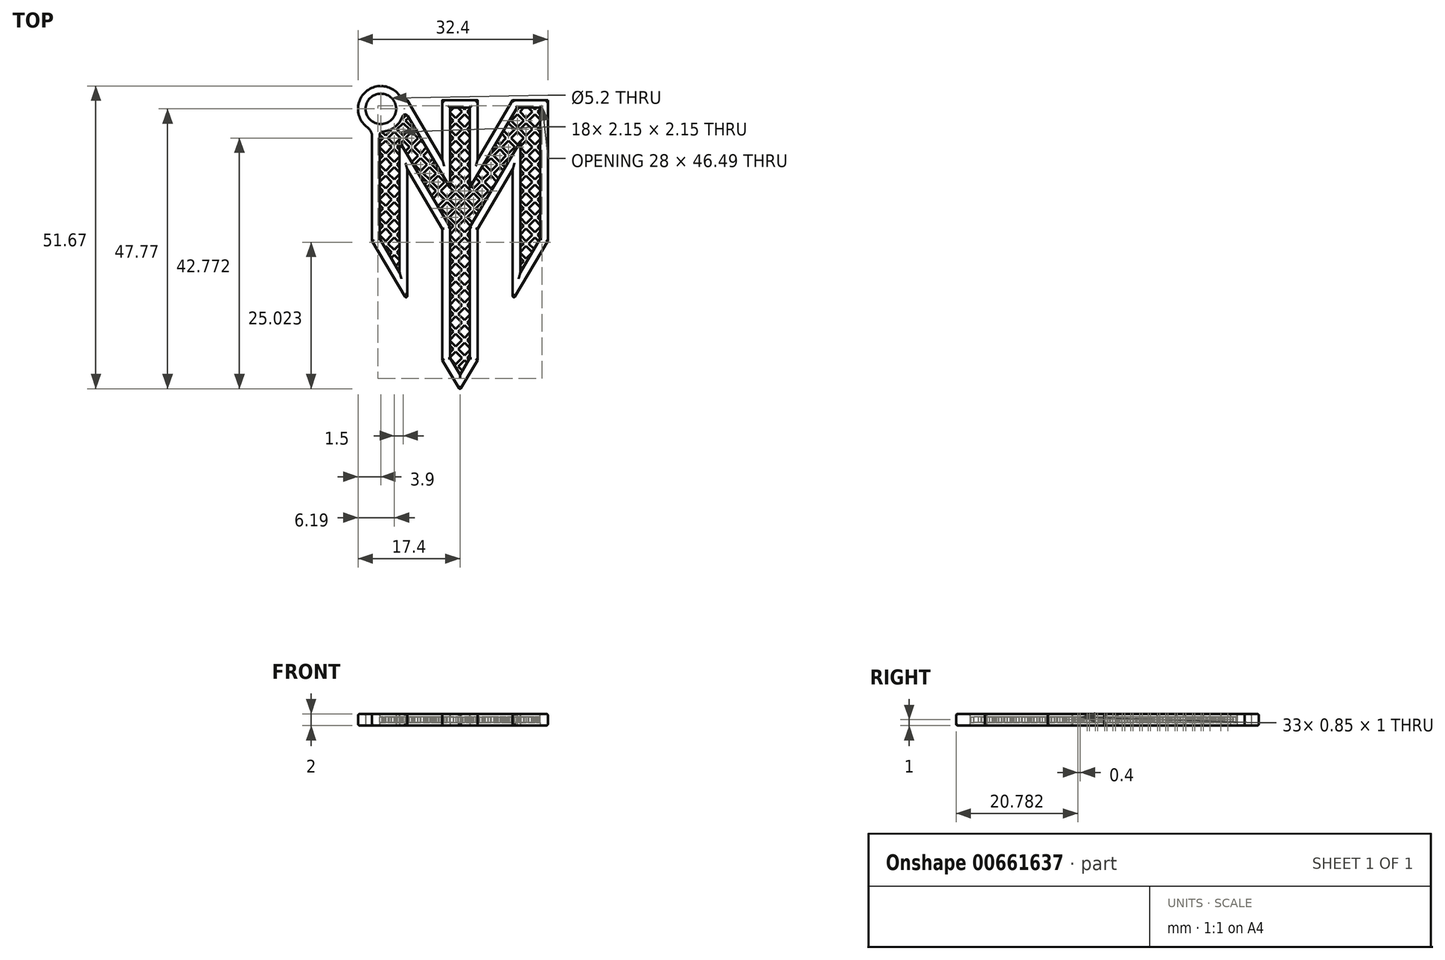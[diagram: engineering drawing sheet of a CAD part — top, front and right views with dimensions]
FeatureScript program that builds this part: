
annotation { "Feature Type Name" : "Feature", "Feature Type Description" : "" }
export const myFeature = defineFeature(function(context is Context, id is Id, definition is map)
    precondition{}
    {
        {
            var Q0;
            Q0=qCreatedBy(makeId("Top.planeOp"),FACE);
            var sketch = newSketch(context, id + "F0", { "sketchPlane" : qUnion([Q0])});
            skLineSegment(sketch, "E0", {"start": v(-3, 0) * mm, "end": v(3, 0) * mm});
            skLineSegment(sketch, "E1", {"start": v(-3, 0) * mm, "end": v(-3, -10.19) * mm});
            skLineSegment(sketch, "E2", {"start": v(-3, -10.19) * mm, "end": v(-9, 0) * mm});
            skLineSegment(sketch, "E3", {"start": v(-9, 0) * mm, "end": v(-15, 0) * mm});
            skLineSegment(sketch, "E4", {"start": v(3, 0) * mm, "end": v(3, -10.19) * mm});
            skLineSegment(sketch, "E5", {"start": v(3, -10.19) * mm, "end": v(9, 0) * mm});
            skLineSegment(sketch, "E6", {"start": v(9, 0) * mm, "end": v(15, 0) * mm});
            skLineSegment(sketch, "E7", {"start": v(0, 0) * mm, "end": v(0, -49.46) * mm, "construction": true});
            skLineSegment(sketch, "E8", {"start": v(-9, 0) * mm, "end": v(-3, 0) * mm, "construction": true});
            skLineSegment(sketch, "E9", {"start": v(3, 0) * mm, "end": v(9, 0) * mm, "construction": true});
            skLineSegment(sketch, "E10", {"start": v(-15, 0) * mm, "end": v(-15, -24) * mm});
            skLineSegment(sketch, "E11", {"start": v(-15, -24) * mm, "end": v(-9, -34.19) * mm});
            skLineSegment(sketch, "E12", {"start": v(-9, -34.19) * mm, "end": v(-9, -11.82) * mm});
            skLineSegment(sketch, "E13", {"start": v(-9, -11.82) * mm, "end": v(-3, -22) * mm});
            skLineSegment(sketch, "E14", {"start": v(-3.83, -8.78) * mm, "end": v(-9, -11.82) * mm, "construction": true});
            skLineSegment(sketch, "E15", {"start": v(15, 0) * mm, "end": v(15, -24) * mm});
            skLineSegment(sketch, "E16", {"start": v(15, -24) * mm, "end": v(9, -34.19) * mm});
            skLineSegment(sketch, "E17", {"start": v(9, -34.19) * mm, "end": v(9, -11.82) * mm});
            skLineSegment(sketch, "E18", {"start": v(9, -11.82) * mm, "end": v(3, -22) * mm});
            skLineSegment(sketch, "E19", {"start": v(-3, -22) * mm, "end": v(-3, -44.37) * mm});
            skLineSegment(sketch, "E20", {"start": v(-3, -44.37) * mm, "end": v(0, -49.46) * mm});
            skLineSegment(sketch, "E21", {"start": v(0, -49.46) * mm, "end": v(3, -44.37) * mm});
            skLineSegment(sketch, "E22", {"start": v(3, -44.37) * mm, "end": v(3, -22) * mm});
            skLineSegment(sketch, "E23", {"start": v(-9, -34.19) * mm, "end": v(-3, -44.37) * mm, "construction": true});
            skLineSegment(sketch, "E24", {"start": v(9, -34.19) * mm, "end": v(3, -44.37) * mm, "construction": true});
            skLineSegment(sketch, "E25", {"start": v(15, 0) * mm, "end": v(15, -6) * mm, "construction": true});
            skLineSegment(sketch, "E26", {"start": v(15, -6) * mm, "end": v(15, -12) * mm, "construction": true});
            skLineSegment(sketch, "E27", {"start": v(15, -12) * mm, "end": v(15, -18) * mm, "construction": true});
            skLineSegment(sketch, "E28", {"start": v(15, -18) * mm, "end": v(15, -24) * mm, "construction": true});
            skCircle(sketch, "E29", {"center": v(-13.5, -1.5) * mm, "radius": 2.6 * mm});
            skCircle(sketch, "E30", {"center": v(-13.5, -1.5) * mm, "radius": 3.9 * mm});
            skLineSegment(sketch, "E31", {"start": v(-13.5, 0) * mm, "end": v(-13.5, -1.5) * mm, "construction": true});
            skLineSegment(sketch, "E32", {"start": v(-15, -1.5) * mm, "end": v(-13.5, -1.5) * mm, "construction": true});
            skLineSegment(sketch, "E33.1", {"start": v(-1.7, -14.95) * mm, "end": v(-9.6, -1.54) * mm});
            skLineSegment(sketch, "E33.2", {"start": v(-1.7, -1.3) * mm, "end": v(-1.7, -14.95) * mm});
            skLineSegment(sketch, "E33.3", {"start": v(-1.7, -1.3) * mm, "end": v(1.7, -1.3) * mm});
            skLineSegment(sketch, "E33.4", {"start": v(1.7, -1.3) * mm, "end": v(1.7, -14.95) * mm});
            skLineSegment(sketch, "E33.5", {"start": v(-13.7, -5.4) * mm, "end": v(-13.7, -23.65) * mm});
            skLineSegment(sketch, "E33.6", {"start": v(1.7, -14.95) * mm, "end": v(9.74, -1.3) * mm});
            skLineSegment(sketch, "E33.7", {"start": v(9.74, -1.3) * mm, "end": v(13.7, -1.3) * mm});
            skLineSegment(sketch, "E33.8", {"start": v(13.7, -1.3) * mm, "end": v(13.7, -6) * mm});
            skLineSegment(sketch, "E33.9", {"start": v(13.7, -6) * mm, "end": v(13.7, -12) * mm});
            skLineSegment(sketch, "E33.10", {"start": v(13.7, -12) * mm, "end": v(13.7, -18) * mm});
            skLineSegment(sketch, "E33.11", {"start": v(13.7, -18) * mm, "end": v(13.7, -23.65) * mm});
            skLineSegment(sketch, "E33.12", {"start": v(-1.7, -21.65) * mm, "end": v(-1.7, -44.02) * mm});
            skLineSegment(sketch, "E33.13", {"start": v(-10.3, -7.05) * mm, "end": v(-1.7, -21.65) * mm});
            skLineSegment(sketch, "E33.14", {"start": v(-10.3, -29.42) * mm, "end": v(-10.3, -7.05) * mm});
            skLineSegment(sketch, "E33.15", {"start": v(-13.7, -23.65) * mm, "end": v(-10.3, -29.42) * mm});
            skLineSegment(sketch, "E33.16", {"start": v(-1.7, -44.02) * mm, "end": v(0, -46.9) * mm});
            skLineSegment(sketch, "E33.17", {"start": v(0, -46.9) * mm, "end": v(1.7, -44.02) * mm});
            skLineSegment(sketch, "E33.18", {"start": v(1.7, -44.02) * mm, "end": v(1.7, -21.65) * mm});
            skLineSegment(sketch, "E33.19", {"start": v(10.3, -7.05) * mm, "end": v(1.7, -21.65) * mm});
            skLineSegment(sketch, "E33.20", {"start": v(10.3, -29.42) * mm, "end": v(10.3, -7.05) * mm});
            skLineSegment(sketch, "E33.21", {"start": v(13.7, -23.65) * mm, "end": v(10.3, -29.42) * mm});
            skSolve(sketch);
        }
        {
            var Q0;
            Q0=makeQuery(id+"F0.imprint","IMPRINT",FACE,{"disambiguationData":[TD([[makeQuery(id+"F0.imprint","IMPRINT",EDGE,{"derivedFrom":sQuery(id+"F0.wireOp",EDGE,"E0")}),-1.0]])]});
            var Q1;
            {var subQ0=sQuery(id+"F0.wireOp",EDGE,"E30");var subQ2=sQuery(id+"F0.wireOp",EDGE,"E3");var subQ3=makeQuery(id+"F0.imprint","INTERSECT",VERTEX,{"derivedFrom":[subQ2,subQ0]});Q1=makeQuery(id+"F0.imprint","IMPRINT",FACE,{"disambiguationData":[TD([[makeQuery(id+"F0.imprint","IMPRINT",EDGE,{"disambiguationData":[TD([[subQ3,-1.0]])],"derivedFrom":subQ2}),1.0]])]});}
            var Q2;
            {var subQ0=sQuery(id+"F0.wireOp",EDGE,"E30");var subQ1=sQuery(id+"F0.wireOp",EDGE,"E3");var subQ2=makeQuery(id+"F0.imprint","INTERSECT",VERTEX,{"derivedFrom":[subQ1,subQ0]});Q2=makeQuery(id+"F0.imprint","IMPRINT",FACE,{"disambiguationData":[TD([[makeQuery(id+"F0.imprint","IMPRINT",EDGE,{"disambiguationData":[TD([[subQ2,-1.0]])],"derivedFrom":subQ1}),-1.0]])]});}
            extrude(context, id + "F1", {"entities" : qUnion([Q0, Q1, Q2]), "depth" : 2 * mm, "offsetDistance" : 25 * mm});
        }
        {
            var Q0;
            Q0=makeQuery(id+"F1.opExtrude","CAP_FACE",FACE,{"disambiguationData":[OSD([sQuery(id+"F0.wireOp",EDGE,"E0"),sQuery(id+"F0.wireOp",EDGE,"E1"),sQuery(id+"F0.wireOp",EDGE,"E2"),sQuery(id+"F0.wireOp",EDGE,"E3"),sQuery(id+"F0.wireOp",EDGE,"E4"),sQuery(id+"F0.wireOp",EDGE,"E5"),sQuery(id+"F0.wireOp",EDGE,"E6"),sQuery(id+"F0.wireOp",EDGE,"E10"),sQuery(id+"F0.wireOp",EDGE,"E11"),sQuery(id+"F0.wireOp",EDGE,"E12"),sQuery(id+"F0.wireOp",EDGE,"E13"),sQuery(id+"F0.wireOp",EDGE,"E15"),sQuery(id+"F0.wireOp",EDGE,"E16"),sQuery(id+"F0.wireOp",EDGE,"E17"),sQuery(id+"F0.wireOp",EDGE,"E18"),sQuery(id+"F0.wireOp",EDGE,"E19"),sQuery(id+"F0.wireOp",EDGE,"E20"),sQuery(id+"F0.wireOp",EDGE,"E21"),sQuery(id+"F0.wireOp",EDGE,"E22"),sQuery(id+"F0.wireOp",EDGE,"E29"),sQuery(id+"F0.wireOp",EDGE,"E30"),sQuery(id+"F0.wireOp",EDGE,"E33.0"),sQuery(id+"F0.wireOp",EDGE,"E33.1"),sQuery(id+"F0.wireOp",EDGE,"E33.2"),sQuery(id+"F0.wireOp",EDGE,"E33.3"),sQuery(id+"F0.wireOp",EDGE,"E33.4"),sQuery(id+"F0.wireOp",EDGE,"E33.5"),sQuery(id+"F0.wireOp",EDGE,"E33.6"),sQuery(id+"F0.wireOp",EDGE,"E33.7"),sQuery(id+"F0.wireOp",EDGE,"E33.8"),sQuery(id+"F0.wireOp",EDGE,"E33.9"),sQuery(id+"F0.wireOp",EDGE,"E33.10"),sQuery(id+"F0.wireOp",EDGE,"E33.11"),sQuery(id+"F0.wireOp",EDGE,"E33.12"),sQuery(id+"F0.wireOp",EDGE,"E33.13"),sQuery(id+"F0.wireOp",EDGE,"E33.14"),sQuery(id+"F0.wireOp",EDGE,"E33.15"),sQuery(id+"F0.wireOp",EDGE,"E33.16"),sQuery(id+"F0.wireOp",EDGE,"E33.17"),sQuery(id+"F0.wireOp",EDGE,"E33.18"),sQuery(id+"F0.wireOp",EDGE,"E33.19"),sQuery(id+"F0.wireOp",EDGE,"E33.20"),sQuery(id+"F0.wireOp",EDGE,"E33.21")])],"isStart":false});
            var sketch = newSketch(context, id + "F2", { "sketchPlane" : qUnion([Q0])});
            skArc(sketch, "E34.0.0", {"start": v(-9.9, 0) * mm, "mid": v(-16.26, 1.26) * mm, "end": v(-15, -5.1) * mm});
            skLineSegment(sketch, "E34.0.1", {"start": v(-15, -5.1) * mm, "end": v(-15, -24) * mm});
            skLineSegment(sketch, "E34.0.2", {"start": v(-15, -24) * mm, "end": v(-9, -34.19) * mm});
            skLineSegment(sketch, "E34.0.3", {"start": v(-9, -34.19) * mm, "end": v(-9, -11.82) * mm});
            skLineSegment(sketch, "E34.0.4", {"start": v(-9, -11.82) * mm, "end": v(-3, -22) * mm});
            skLineSegment(sketch, "E34.0.5", {"start": v(-3, -22) * mm, "end": v(-3, -44.37) * mm});
            skLineSegment(sketch, "E34.0.6", {"start": v(-3, -44.37) * mm, "end": v(0, -49.46) * mm});
            skLineSegment(sketch, "E34.0.7", {"start": v(0, -49.46) * mm, "end": v(3, -44.37) * mm});
            skLineSegment(sketch, "E34.0.8", {"start": v(3, -44.37) * mm, "end": v(3, -22) * mm});
            skLineSegment(sketch, "E34.0.9", {"start": v(3, -22) * mm, "end": v(9, -11.82) * mm});
            skLineSegment(sketch, "E34.0.10", {"start": v(9, -11.82) * mm, "end": v(9, -34.19) * mm});
            skLineSegment(sketch, "E34.0.11", {"start": v(9, -34.19) * mm, "end": v(15, -24) * mm});
            skLineSegment(sketch, "E34.0.12", {"start": v(15, -24) * mm, "end": v(15, 0) * mm});
            skLineSegment(sketch, "E34.0.13", {"start": v(15, 0) * mm, "end": v(9, 0) * mm});
            skLineSegment(sketch, "E34.0.14", {"start": v(9, 0) * mm, "end": v(3, -10.19) * mm});
            skLineSegment(sketch, "E34.0.15", {"start": v(3, -10.19) * mm, "end": v(3, 0) * mm});
            skLineSegment(sketch, "E34.0.16", {"start": v(3, 0) * mm, "end": v(-3, 0) * mm});
            skLineSegment(sketch, "E34.0.17", {"start": v(-3, 0) * mm, "end": v(-3, -10.19) * mm});
            skLineSegment(sketch, "E34.0.18", {"start": v(-3, -10.19) * mm, "end": v(-9, 0) * mm});
            skLineSegment(sketch, "E34.0.19", {"start": v(-9, 0) * mm, "end": v(-9.9, 0) * mm});
            skSolve(sketch);
        }
        {
            var Q0;
            Q0=makeQuery(id+"F1.opExtrude","SWEPT_EDGE",EDGE,{"disambiguationData":[OSD([sQuery(id+"F0.wireOp",EDGE,"E3"),sQuery(id+"F0.wireOp",EDGE,"E30")])]});
            var Q1;
            Q1=makeQuery(id+"F1.opExtrude","SWEPT_EDGE",EDGE,{"disambiguationData":[OSD([sQuery(id+"F0.wireOp",EDGE,"E10"),sQuery(id+"F0.wireOp",EDGE,"E30")])]});
            fillet(context, id + "F3", {"entities" : qUnion([Q0, Q1]), "radius" : 2 * mm, "tangentPropagation" : true, "defaultsChanged" : false, "vertexSettings" : [], "allowEdgeOverflow" : false});
        }
        {
            var Q0;
            Q0=makeQuery(id+"F1.opExtrude","SWEPT_EDGE",EDGE,{"disambiguationData":[OSD([sQuery(id+"F0.wireOp",EDGE,"E11"),sQuery(id+"F0.wireOp",EDGE,"E12")])]});
            var Q1;
            Q1=makeQuery(id+"F1.opExtrude","SWEPT_EDGE",EDGE,{"disambiguationData":[OSD([sQuery(id+"F0.wireOp",EDGE,"E16"),sQuery(id+"F0.wireOp",EDGE,"E17")])]});
            var Q2;
            Q2=makeQuery(id+"F1.opExtrude","SWEPT_EDGE",EDGE,{"disambiguationData":[OSD([sQuery(id+"F0.wireOp",EDGE,"E20"),sQuery(id+"F0.wireOp",EDGE,"E21")])]});
            fillet(context, id + "F4", {"entities" : qUnion([Q0, Q1, Q2]), "tangentPropagation" : true, "radius" : 0.2 * mm, "defaultsChanged" : false, "vertexSettings" : [], "allowEdgeOverflow" : false});
        }
        {
            var Q0;
            Q0=makeQuery(id+"F1.opExtrude","CAP_FACE",FACE,{"disambiguationData":[OSD([sQuery(id+"F0.wireOp",EDGE,"E0"),sQuery(id+"F0.wireOp",EDGE,"E1"),sQuery(id+"F0.wireOp",EDGE,"E2"),sQuery(id+"F0.wireOp",EDGE,"E3"),sQuery(id+"F0.wireOp",EDGE,"E4"),sQuery(id+"F0.wireOp",EDGE,"E5"),sQuery(id+"F0.wireOp",EDGE,"E6"),sQuery(id+"F0.wireOp",EDGE,"E10"),sQuery(id+"F0.wireOp",EDGE,"E11"),sQuery(id+"F0.wireOp",EDGE,"E12"),sQuery(id+"F0.wireOp",EDGE,"E13"),sQuery(id+"F0.wireOp",EDGE,"E15"),sQuery(id+"F0.wireOp",EDGE,"E16"),sQuery(id+"F0.wireOp",EDGE,"E17"),sQuery(id+"F0.wireOp",EDGE,"E18"),sQuery(id+"F0.wireOp",EDGE,"E19"),sQuery(id+"F0.wireOp",EDGE,"E20"),sQuery(id+"F0.wireOp",EDGE,"E21"),sQuery(id+"F0.wireOp",EDGE,"E22"),sQuery(id+"F0.wireOp",EDGE,"E29"),sQuery(id+"F0.wireOp",EDGE,"E30"),sQuery(id+"F0.wireOp",EDGE,"E33.0"),sQuery(id+"F0.wireOp",EDGE,"E33.1"),sQuery(id+"F0.wireOp",EDGE,"E33.2"),sQuery(id+"F0.wireOp",EDGE,"E33.3"),sQuery(id+"F0.wireOp",EDGE,"E33.4"),sQuery(id+"F0.wireOp",EDGE,"E33.5"),sQuery(id+"F0.wireOp",EDGE,"E33.6"),sQuery(id+"F0.wireOp",EDGE,"E33.7"),sQuery(id+"F0.wireOp",EDGE,"E33.8"),sQuery(id+"F0.wireOp",EDGE,"E33.9"),sQuery(id+"F0.wireOp",EDGE,"E33.10"),sQuery(id+"F0.wireOp",EDGE,"E33.11"),sQuery(id+"F0.wireOp",EDGE,"E33.12"),sQuery(id+"F0.wireOp",EDGE,"E33.13"),sQuery(id+"F0.wireOp",EDGE,"E33.14"),sQuery(id+"F0.wireOp",EDGE,"E33.15"),sQuery(id+"F0.wireOp",EDGE,"E33.16"),sQuery(id+"F0.wireOp",EDGE,"E33.17"),sQuery(id+"F0.wireOp",EDGE,"E33.18"),sQuery(id+"F0.wireOp",EDGE,"E33.19"),sQuery(id+"F0.wireOp",EDGE,"E33.20"),sQuery(id+"F0.wireOp",EDGE,"E33.21")])],"isStart":false});
            var sketch = newSketch(context, id + "F5", { "sketchPlane" : qUnion([Q0])});
            skLineSegment(sketch, "E35.0.0", {"start": v(-15, -24) * mm, "end": v(-9.37, -33.55) * mm});
            skArc(sketch, "E35.0.1", {"start": v(-9.37, -33.55) * mm, "mid": v(-9.15, -33.65) * mm, "end": v(-9, -33.45) * mm});
            skLineSegment(sketch, "E35.0.2", {"start": v(-9, -33.45) * mm, "end": v(-9, -11.82) * mm});
            skLineSegment(sketch, "E35.0.3", {"start": v(-9, -11.82) * mm, "end": v(-3, -22) * mm});
            skLineSegment(sketch, "E35.0.4", {"start": v(-3, -22) * mm, "end": v(-3, -44.37) * mm});
            skLineSegment(sketch, "E35.0.5", {"start": v(-3, -44.37) * mm, "end": v(-0.17, -49.17) * mm});
            skArc(sketch, "E35.0.6", {"start": v(-0.17, -49.17) * mm, "mid": v(0, -49.27) * mm, "end": v(0.17, -49.17) * mm});
            skLineSegment(sketch, "E35.0.7", {"start": v(0.17, -49.17) * mm, "end": v(3, -44.37) * mm});
            skLineSegment(sketch, "E35.0.8", {"start": v(3, -44.37) * mm, "end": v(3, -22) * mm});
            skLineSegment(sketch, "E35.0.9", {"start": v(3, -22) * mm, "end": v(9, -11.82) * mm});
            skLineSegment(sketch, "E35.0.10", {"start": v(9, -11.82) * mm, "end": v(9, -33.45) * mm});
            skArc(sketch, "E35.0.11", {"start": v(9, -33.45) * mm, "mid": v(9.15, -33.65) * mm, "end": v(9.37, -33.55) * mm});
            skLineSegment(sketch, "E35.0.12", {"start": v(9.37, -33.55) * mm, "end": v(15, -24) * mm});
            skLineSegment(sketch, "E35.0.13", {"start": v(15, -24) * mm, "end": v(15, 0) * mm});
            skLineSegment(sketch, "E35.0.14", {"start": v(15, 0) * mm, "end": v(9, 0) * mm});
            skLineSegment(sketch, "E35.0.15", {"start": v(9, 0) * mm, "end": v(3, -10.19) * mm});
            skLineSegment(sketch, "E35.0.16", {"start": v(3, -10.19) * mm, "end": v(3, 0) * mm});
            skLineSegment(sketch, "E35.0.17", {"start": v(3, 0) * mm, "end": v(-3, 0) * mm});
            skLineSegment(sketch, "E35.0.18", {"start": v(-3, 0) * mm, "end": v(-3, -10.19) * mm});
            skLineSegment(sketch, "E35.0.19", {"start": v(-3, -10.19) * mm, "end": v(-9, 0) * mm});
            skArc(sketch, "E35.0.20", {"start": v(-9, 0) * mm, "mid": v(-9.76, 0.26) * mm, "end": v(-10.35, 0.8) * mm});
            skArc(sketch, "E35.0.21", {"start": v(-10.35, 0.8) * mm, "mid": v(-16.25, 1.26) * mm, "end": v(-15.81, -4.64) * mm});
            skArc(sketch, "E35.0.22", {"start": v(-15.81, -4.64) * mm, "mid": v(-15.21, -5.35) * mm, "end": v(-15, -6.25) * mm});
            skLineSegment(sketch, "E35.0.23", {"start": v(-15, -6.25) * mm, "end": v(-15, -24) * mm});
            skLineSegment(sketch, "E36", {"start": v(1.83, -50.61) * mm, "end": v(-51.76, 2.97) * mm});
            skLineSegment(sketch, "E37", {"start": v(-52.83, 3.2) * mm, "end": v(1.75, -51.38) * mm});
            skLineSegment(sketch, "E38.1.0.0", {"start": v(-49.83, 3.2) * mm, "end": v(4.75, -51.38) * mm});
            skLineSegment(sketch, "E38.1.0.1", {"start": v(4.83, -50.61) * mm, "end": v(-48.76, 2.97) * mm});
            skLineSegment(sketch, "E38.2.0.0", {"start": v(-46.83, 3.2) * mm, "end": v(7.75, -51.38) * mm});
            skLineSegment(sketch, "E38.2.0.1", {"start": v(7.83, -50.61) * mm, "end": v(-45.76, 2.97) * mm});
            skLineSegment(sketch, "E38.3.0.0", {"start": v(-43.83, 3.2) * mm, "end": v(10.75, -51.38) * mm});
            skLineSegment(sketch, "E38.3.0.1", {"start": v(10.83, -50.61) * mm, "end": v(-42.76, 2.97) * mm});
            skLineSegment(sketch, "E38.4.0.0", {"start": v(-40.83, 3.2) * mm, "end": v(13.75, -51.38) * mm});
            skLineSegment(sketch, "E38.4.0.1", {"start": v(13.83, -50.61) * mm, "end": v(-39.76, 2.97) * mm});
            skLineSegment(sketch, "E38.5.0.0", {"start": v(-37.83, 3.2) * mm, "end": v(16.75, -51.38) * mm});
            skLineSegment(sketch, "E38.5.0.1", {"start": v(16.83, -50.61) * mm, "end": v(-36.76, 2.97) * mm});
            skLineSegment(sketch, "E38.6.0.0", {"start": v(-34.83, 3.2) * mm, "end": v(19.75, -51.38) * mm});
            skLineSegment(sketch, "E38.6.0.1", {"start": v(19.83, -50.61) * mm, "end": v(-33.76, 2.97) * mm});
            skLineSegment(sketch, "E38.7.0.0", {"start": v(-31.83, 3.2) * mm, "end": v(22.75, -51.38) * mm});
            skLineSegment(sketch, "E38.7.0.1", {"start": v(22.83, -50.61) * mm, "end": v(-30.76, 2.97) * mm});
            skLineSegment(sketch, "E38.8.0.0", {"start": v(-28.83, 3.2) * mm, "end": v(25.75, -51.38) * mm});
            skLineSegment(sketch, "E38.8.0.1", {"start": v(25.83, -50.61) * mm, "end": v(-27.76, 2.97) * mm});
            skLineSegment(sketch, "E38.9.0.0", {"start": v(-25.83, 3.2) * mm, "end": v(28.75, -51.38) * mm});
            skLineSegment(sketch, "E38.9.0.1", {"start": v(28.83, -50.61) * mm, "end": v(-24.76, 2.97) * mm});
            skLineSegment(sketch, "E38.10.0.0", {"start": v(-22.83, 3.2) * mm, "end": v(31.75, -51.38) * mm});
            skLineSegment(sketch, "E38.10.0.1", {"start": v(31.83, -50.61) * mm, "end": v(-21.76, 2.97) * mm});
            skLineSegment(sketch, "E38.11.0.0", {"start": v(-19.83, 3.2) * mm, "end": v(34.75, -51.38) * mm});
            skLineSegment(sketch, "E38.11.0.1", {"start": v(34.83, -50.61) * mm, "end": v(-18.76, 2.97) * mm});
            skLineSegment(sketch, "E38.12.0.0", {"start": v(-16.83, 3.2) * mm, "end": v(37.75, -51.38) * mm});
            skLineSegment(sketch, "E38.12.0.1", {"start": v(37.83, -50.61) * mm, "end": v(-15.76, 2.97) * mm});
            skLineSegment(sketch, "E38.13.0.0", {"start": v(-13.83, 3.2) * mm, "end": v(40.75, -51.38) * mm});
            skLineSegment(sketch, "E38.13.0.1", {"start": v(40.83, -50.61) * mm, "end": v(-12.76, 2.97) * mm});
            skLineSegment(sketch, "E38.14.0.0", {"start": v(-10.83, 3.2) * mm, "end": v(43.75, -51.38) * mm});
            skLineSegment(sketch, "E38.14.0.1", {"start": v(43.83, -50.61) * mm, "end": v(-9.76, 2.97) * mm});
            skLineSegment(sketch, "E38.15.0.0", {"start": v(-7.83, 3.2) * mm, "end": v(46.75, -51.38) * mm});
            skLineSegment(sketch, "E38.15.0.1", {"start": v(46.83, -50.61) * mm, "end": v(-6.76, 2.97) * mm});
            skLineSegment(sketch, "E38.16.0.0", {"start": v(-4.83, 3.2) * mm, "end": v(49.75, -51.38) * mm});
            skLineSegment(sketch, "E38.16.0.1", {"start": v(49.83, -50.61) * mm, "end": v(-3.76, 2.97) * mm});
            skLineSegment(sketch, "E38.17.0.0", {"start": v(-1.83, 3.2) * mm, "end": v(52.75, -51.38) * mm});
            skLineSegment(sketch, "E38.17.0.1", {"start": v(52.83, -50.61) * mm, "end": v(-0.76, 2.97) * mm});
            skLineSegment(sketch, "E38.18.0.0", {"start": v(1.17, 3.2) * mm, "end": v(55.75, -51.38) * mm});
            skLineSegment(sketch, "E38.18.0.1", {"start": v(55.83, -50.61) * mm, "end": v(2.24, 2.97) * mm});
            skLineSegment(sketch, "E38.19.0.0", {"start": v(4.17, 3.2) * mm, "end": v(58.75, -51.38) * mm});
            skLineSegment(sketch, "E38.19.0.1", {"start": v(58.83, -50.61) * mm, "end": v(5.24, 2.97) * mm});
            skLineSegment(sketch, "E38.direction1", {"start": v(1.75, -51.38) * mm, "end": v(4.75, -51.38) * mm, "construction": true});
            skLineSegment(sketch, "E39.0.20.0", {"start": v(7.17, 3.2) * mm, "end": v(61.75, -51.38) * mm});
            skLineSegment(sketch, "E39.3.20.0", {"start": v(61.83, -50.61) * mm, "end": v(8.24, 2.97) * mm});
            skLineSegment(sketch, "E40.0.21.0", {"start": v(10.17, 3.2) * mm, "end": v(64.75, -51.38) * mm});
            skLineSegment(sketch, "E40.3.21.0", {"start": v(64.83, -50.61) * mm, "end": v(11.24, 2.97) * mm});
            skSolve(sketch);
        }
        {
            var Q0;
            Q0=makeQuery(id+"F1.opExtrude","CAP_FACE",FACE,{"disambiguationData":[OSD([sQuery(id+"F0.wireOp",EDGE,"E0"),sQuery(id+"F0.wireOp",EDGE,"E1"),sQuery(id+"F0.wireOp",EDGE,"E2"),sQuery(id+"F0.wireOp",EDGE,"E3"),sQuery(id+"F0.wireOp",EDGE,"E4"),sQuery(id+"F0.wireOp",EDGE,"E5"),sQuery(id+"F0.wireOp",EDGE,"E6"),sQuery(id+"F0.wireOp",EDGE,"E10"),sQuery(id+"F0.wireOp",EDGE,"E11"),sQuery(id+"F0.wireOp",EDGE,"E12"),sQuery(id+"F0.wireOp",EDGE,"E13"),sQuery(id+"F0.wireOp",EDGE,"E15"),sQuery(id+"F0.wireOp",EDGE,"E16"),sQuery(id+"F0.wireOp",EDGE,"E17"),sQuery(id+"F0.wireOp",EDGE,"E18"),sQuery(id+"F0.wireOp",EDGE,"E19"),sQuery(id+"F0.wireOp",EDGE,"E20"),sQuery(id+"F0.wireOp",EDGE,"E21"),sQuery(id+"F0.wireOp",EDGE,"E22"),sQuery(id+"F0.wireOp",EDGE,"E29"),sQuery(id+"F0.wireOp",EDGE,"E30"),sQuery(id+"F0.wireOp",EDGE,"E33.0"),sQuery(id+"F0.wireOp",EDGE,"E33.1"),sQuery(id+"F0.wireOp",EDGE,"E33.2"),sQuery(id+"F0.wireOp",EDGE,"E33.3"),sQuery(id+"F0.wireOp",EDGE,"E33.4"),sQuery(id+"F0.wireOp",EDGE,"E33.5"),sQuery(id+"F0.wireOp",EDGE,"E33.6"),sQuery(id+"F0.wireOp",EDGE,"E33.7"),sQuery(id+"F0.wireOp",EDGE,"E33.8"),sQuery(id+"F0.wireOp",EDGE,"E33.9"),sQuery(id+"F0.wireOp",EDGE,"E33.10"),sQuery(id+"F0.wireOp",EDGE,"E33.11"),sQuery(id+"F0.wireOp",EDGE,"E33.12"),sQuery(id+"F0.wireOp",EDGE,"E33.13"),sQuery(id+"F0.wireOp",EDGE,"E33.14"),sQuery(id+"F0.wireOp",EDGE,"E33.15"),sQuery(id+"F0.wireOp",EDGE,"E33.16"),sQuery(id+"F0.wireOp",EDGE,"E33.17"),sQuery(id+"F0.wireOp",EDGE,"E33.18"),sQuery(id+"F0.wireOp",EDGE,"E33.19"),sQuery(id+"F0.wireOp",EDGE,"E33.20"),sQuery(id+"F0.wireOp",EDGE,"E33.21")])],"isStart":false});
            var sketch = newSketch(context, id + "F6", { "sketchPlane" : qUnion([Q0])});
            skLineSegment(sketch, "E41", {"start": v(0.42, -50.8) * mm, "end": v(54.44, 3.23) * mm});
            skLineSegment(sketch, "E42", {"start": v(-0.94, -51.3) * mm, "end": v(53.97, 3.6) * mm});
            skLineSegment(sketch, "E43.1.0.0", {"start": v(-3.94, -51.3) * mm, "end": v(50.97, 3.6) * mm});
            skLineSegment(sketch, "E43.1.0.1", {"start": v(-2.58, -50.8) * mm, "end": v(51.44, 3.23) * mm});
            skLineSegment(sketch, "E43.2.0.0", {"start": v(-6.94, -51.3) * mm, "end": v(47.97, 3.6) * mm});
            skLineSegment(sketch, "E43.2.0.1", {"start": v(-5.58, -50.8) * mm, "end": v(48.44, 3.23) * mm});
            skLineSegment(sketch, "E43.3.0.0", {"start": v(-9.94, -51.3) * mm, "end": v(44.97, 3.6) * mm});
            skLineSegment(sketch, "E43.3.0.1", {"start": v(-8.58, -50.8) * mm, "end": v(45.44, 3.23) * mm});
            skLineSegment(sketch, "E43.4.0.0", {"start": v(-12.94, -51.3) * mm, "end": v(41.97, 3.6) * mm});
            skLineSegment(sketch, "E43.4.0.1", {"start": v(-11.58, -50.8) * mm, "end": v(42.44, 3.23) * mm});
            skLineSegment(sketch, "E43.5.0.0", {"start": v(-15.94, -51.3) * mm, "end": v(38.97, 3.6) * mm});
            skLineSegment(sketch, "E43.5.0.1", {"start": v(-14.58, -50.8) * mm, "end": v(39.44, 3.23) * mm});
            skLineSegment(sketch, "E43.6.0.0", {"start": v(-18.94, -51.3) * mm, "end": v(35.97, 3.6) * mm});
            skLineSegment(sketch, "E43.6.0.1", {"start": v(-17.58, -50.8) * mm, "end": v(36.44, 3.23) * mm});
            skLineSegment(sketch, "E43.7.0.0", {"start": v(-21.94, -51.3) * mm, "end": v(32.97, 3.6) * mm});
            skLineSegment(sketch, "E43.7.0.1", {"start": v(-20.58, -50.8) * mm, "end": v(33.44, 3.23) * mm});
            skLineSegment(sketch, "E43.8.0.0", {"start": v(-24.94, -51.3) * mm, "end": v(29.97, 3.6) * mm});
            skLineSegment(sketch, "E43.8.0.1", {"start": v(-23.58, -50.8) * mm, "end": v(30.44, 3.23) * mm});
            skLineSegment(sketch, "E43.9.0.0", {"start": v(-27.94, -51.3) * mm, "end": v(26.97, 3.6) * mm});
            skLineSegment(sketch, "E43.9.0.1", {"start": v(-26.58, -50.8) * mm, "end": v(27.44, 3.23) * mm});
            skLineSegment(sketch, "E43.10.0.0", {"start": v(-30.94, -51.3) * mm, "end": v(23.97, 3.6) * mm});
            skLineSegment(sketch, "E43.10.0.1", {"start": v(-29.58, -50.8) * mm, "end": v(24.44, 3.23) * mm});
            skLineSegment(sketch, "E43.11.0.0", {"start": v(-33.94, -51.3) * mm, "end": v(20.97, 3.6) * mm});
            skLineSegment(sketch, "E43.11.0.1", {"start": v(-32.58, -50.8) * mm, "end": v(21.44, 3.23) * mm});
            skLineSegment(sketch, "E43.12.0.0", {"start": v(-36.94, -51.3) * mm, "end": v(17.97, 3.6) * mm});
            skLineSegment(sketch, "E43.12.0.1", {"start": v(-35.58, -50.8) * mm, "end": v(18.44, 3.23) * mm});
            skLineSegment(sketch, "E43.13.0.0", {"start": v(-39.94, -51.3) * mm, "end": v(14.97, 3.6) * mm});
            skLineSegment(sketch, "E43.13.0.1", {"start": v(-38.58, -50.8) * mm, "end": v(15.44, 3.23) * mm});
            skLineSegment(sketch, "E43.14.0.0", {"start": v(-42.94, -51.3) * mm, "end": v(11.97, 3.6) * mm});
            skLineSegment(sketch, "E43.14.0.1", {"start": v(-41.58, -50.8) * mm, "end": v(12.44, 3.23) * mm});
            skLineSegment(sketch, "E43.15.0.0", {"start": v(-45.94, -51.3) * mm, "end": v(8.97, 3.6) * mm});
            skLineSegment(sketch, "E43.15.0.1", {"start": v(-44.58, -50.8) * mm, "end": v(9.44, 3.23) * mm});
            skLineSegment(sketch, "E43.16.0.0", {"start": v(-48.94, -51.3) * mm, "end": v(5.97, 3.6) * mm});
            skLineSegment(sketch, "E43.16.0.1", {"start": v(-47.58, -50.8) * mm, "end": v(6.44, 3.23) * mm});
            skLineSegment(sketch, "E43.17.0.0", {"start": v(-51.94, -51.3) * mm, "end": v(2.97, 3.6) * mm});
            skLineSegment(sketch, "E43.17.0.1", {"start": v(-50.58, -50.8) * mm, "end": v(3.44, 3.23) * mm});
            skLineSegment(sketch, "E43.18.0.0", {"start": v(-54.94, -51.3) * mm, "end": v(-0.03, 3.6) * mm});
            skLineSegment(sketch, "E43.18.0.1", {"start": v(-53.58, -50.8) * mm, "end": v(0.44, 3.23) * mm});
            skLineSegment(sketch, "E43.19.0.0", {"start": v(-57.94, -51.3) * mm, "end": v(-3.03, 3.6) * mm});
            skLineSegment(sketch, "E43.19.0.1", {"start": v(-56.58, -50.8) * mm, "end": v(-2.56, 3.23) * mm});
            skLineSegment(sketch, "E43.direction1", {"start": v(-0.94, -51.3) * mm, "end": v(-3.94, -51.3) * mm, "construction": true});
            skLineSegment(sketch, "E44.0.20.0", {"start": v(-60.94, -51.3) * mm, "end": v(-6.03, 3.6) * mm});
            skLineSegment(sketch, "E44.3.20.0", {"start": v(-59.58, -50.8) * mm, "end": v(-5.56, 3.23) * mm});
            skLineSegment(sketch, "E44.0.21.0", {"start": v(-63.94, -51.3) * mm, "end": v(-9.03, 3.6) * mm});
            skLineSegment(sketch, "E44.3.21.0", {"start": v(-62.58, -50.8) * mm, "end": v(-8.56, 3.23) * mm});
            skSolve(sketch);
        }
        {
            var Q0;
            {var subQ0=sQuery(id+"F5.wireOp",EDGE,"E38.10.0.0");var subQ1=makeQuery(id+"F1.opExtrude","CAP_EDGE",EDGE,{"disambiguationData":[OSD([sQuery(id+"F0.wireOp",EDGE,"E33.5")])],"isStart":false});var subQ2=makeQuery(id+"F5.imprint","INTERSECT",VERTEX,{"derivedFrom":[subQ1,subQ0]});Q0=makeQuery(id+"F5.imprint","IMPRINT",FACE,{"disambiguationData":[TD([[makeQuery(id+"F5.imprint","IMPRINT",EDGE,{"disambiguationData":[TD([[subQ2,-1.0]])],"derivedFrom":subQ0}),1.0]])]});}
            var Q1;
            {var subQ0=sQuery(id+"F5.wireOp",EDGE,"E38.9.0.0");var subQ1=makeQuery(id+"F1.opExtrude","CAP_EDGE",EDGE,{"disambiguationData":[OSD([sQuery(id+"F0.wireOp",EDGE,"E33.5")])],"isStart":false});var subQ2=makeQuery(id+"F5.imprint","INTERSECT",VERTEX,{"derivedFrom":[subQ1,subQ0]});Q1=makeQuery(id+"F5.imprint","IMPRINT",FACE,{"disambiguationData":[TD([[makeQuery(id+"F5.imprint","IMPRINT",EDGE,{"disambiguationData":[TD([[subQ2,-1.0]])],"derivedFrom":subQ0}),1.0]])]});}
            var Q2;
            {var subQ0=sQuery(id+"F5.wireOp",EDGE,"E38.8.0.0");var subQ1=makeQuery(id+"F1.opExtrude","CAP_EDGE",EDGE,{"disambiguationData":[OSD([sQuery(id+"F0.wireOp",EDGE,"E33.5")])],"isStart":false});var subQ2=makeQuery(id+"F5.imprint","INTERSECT",VERTEX,{"derivedFrom":[subQ1,subQ0]});Q2=makeQuery(id+"F5.imprint","IMPRINT",FACE,{"disambiguationData":[TD([[makeQuery(id+"F5.imprint","IMPRINT",EDGE,{"disambiguationData":[TD([[subQ2,-1.0]])],"derivedFrom":subQ0}),1.0]])]});}
            var Q3;
            {var subQ0=sQuery(id+"F5.wireOp",EDGE,"E38.11.0.0");var subQ4=makeQuery(id+"F1.opExtrude","CAP_EDGE",EDGE,{"disambiguationData":[OSD([sQuery(id+"F0.wireOp",EDGE,"E33.19")])],"isStart":false});var subQ5=makeQuery(id+"F5.imprint","INTERSECT",VERTEX,{"derivedFrom":[subQ4,subQ0]});Q3=makeQuery(id+"F5.imprint","IMPRINT",FACE,{"disambiguationData":[TD([[makeQuery(id+"F5.imprint","IMPRINT",EDGE,{"disambiguationData":[TD([[subQ5,1.0]])],"derivedFrom":subQ4}),-1.0]])]});}
            var Q4;
            {var subQ0=sQuery(id+"F5.wireOp",EDGE,"E38.12.0.0");var subQ4=makeQuery(id+"F1.opExtrude","CAP_EDGE",EDGE,{"disambiguationData":[OSD([sQuery(id+"F0.wireOp",EDGE,"E33.1")])],"isStart":false});var subQ5=makeQuery(id+"F5.imprint","INTERSECT",VERTEX,{"derivedFrom":[subQ4,subQ0]});Q4=makeQuery(id+"F5.imprint","IMPRINT",FACE,{"disambiguationData":[TD([[makeQuery(id+"F5.imprint","IMPRINT",EDGE,{"disambiguationData":[TD([[subQ5,-1.0]])],"derivedFrom":subQ4}),1.0]])]});}
            var Q5;
            {var subQ5=makeQuery(id+"F1.opExtrude","CAP_EDGE",EDGE,{"disambiguationData":[OSD([sQuery(id+"F0.wireOp",EDGE,"E33.13")])],"isStart":false});var subQ7=sQuery(id+"F5.wireOp",EDGE,"E38.10.0.0");var subQ8=makeQuery(id+"F5.imprint","INTERSECT",VERTEX,{"derivedFrom":[subQ5,subQ7]});Q5=makeQuery(id+"F5.imprint","IMPRINT",FACE,{"disambiguationData":[TD([[makeQuery(id+"F5.imprint","IMPRINT",EDGE,{"disambiguationData":[TD([[subQ8,-1.0]])],"derivedFrom":subQ7}),1.0]])]});}
            var Q6;
            {var subQ0=sQuery(id+"F5.wireOp",EDGE,"E38.7.0.0");var subQ1=makeQuery(id+"F1.opExtrude","CAP_EDGE",EDGE,{"disambiguationData":[OSD([sQuery(id+"F0.wireOp",EDGE,"E33.5")])],"isStart":false});var subQ2=makeQuery(id+"F5.imprint","INTERSECT",VERTEX,{"derivedFrom":[subQ1,subQ0]});Q6=makeQuery(id+"F5.imprint","IMPRINT",FACE,{"disambiguationData":[TD([[makeQuery(id+"F5.imprint","IMPRINT",EDGE,{"disambiguationData":[TD([[subQ2,-1.0]])],"derivedFrom":subQ0}),1.0]])]});}
            var Q7;
            {var subQ0=sQuery(id+"F5.wireOp",EDGE,"E38.6.0.0");var subQ1=makeQuery(id+"F1.opExtrude","CAP_EDGE",EDGE,{"disambiguationData":[OSD([sQuery(id+"F0.wireOp",EDGE,"E33.5")])],"isStart":false});var subQ2=makeQuery(id+"F5.imprint","INTERSECT",VERTEX,{"derivedFrom":[subQ1,subQ0]});Q7=makeQuery(id+"F5.imprint","IMPRINT",FACE,{"disambiguationData":[TD([[makeQuery(id+"F5.imprint","IMPRINT",EDGE,{"disambiguationData":[TD([[subQ2,-1.0]])],"derivedFrom":subQ0}),1.0]])]});}
            var Q8;
            {var subQ0=sQuery(id+"F5.wireOp",EDGE,"E38.5.0.0");var subQ1=makeQuery(id+"F1.opExtrude","CAP_EDGE",EDGE,{"disambiguationData":[OSD([sQuery(id+"F0.wireOp",EDGE,"E33.5")])],"isStart":false});var subQ2=makeQuery(id+"F5.imprint","INTERSECT",VERTEX,{"derivedFrom":[subQ1,subQ0]});Q8=makeQuery(id+"F5.imprint","IMPRINT",FACE,{"disambiguationData":[TD([[makeQuery(id+"F5.imprint","IMPRINT",EDGE,{"disambiguationData":[TD([[subQ2,-1.0]])],"derivedFrom":subQ0}),1.0]])]});}
            var Q9;
            {var subQ0=sQuery(id+"F5.wireOp",EDGE,"E38.4.0.0");var subQ1=makeQuery(id+"F1.opExtrude","CAP_EDGE",EDGE,{"disambiguationData":[OSD([sQuery(id+"F0.wireOp",EDGE,"E33.15")])],"isStart":false});var subQ2=makeQuery(id+"F5.imprint","INTERSECT",VERTEX,{"derivedFrom":[subQ1,subQ0]});Q9=makeQuery(id+"F5.imprint","IMPRINT",FACE,{"disambiguationData":[TD([[makeQuery(id+"F5.imprint","IMPRINT",EDGE,{"disambiguationData":[TD([[subQ2,-1.0]])],"derivedFrom":subQ0}),1.0]])]});}
            var Q10;
            {var subQ0=sQuery(id+"F5.wireOp",EDGE,"E38.15.0.0");var subQ1=makeQuery(id+"F1.opExtrude","CAP_EDGE",EDGE,{"disambiguationData":[OSD([sQuery(id+"F0.wireOp",EDGE,"E33.2")])],"isStart":false});var subQ2=makeQuery(id+"F5.imprint","INTERSECT",VERTEX,{"derivedFrom":[subQ1,subQ0]});Q10=makeQuery(id+"F5.imprint","IMPRINT",FACE,{"disambiguationData":[TD([[makeQuery(id+"F5.imprint","IMPRINT",EDGE,{"disambiguationData":[TD([[subQ2,-1.0]])],"derivedFrom":subQ0}),1.0]])]});}
            var Q11;
            {var subQ0=sQuery(id+"F5.wireOp",EDGE,"E38.16.0.0");var subQ1=makeQuery(id+"F1.opExtrude","CAP_EDGE",EDGE,{"disambiguationData":[OSD([sQuery(id+"F0.wireOp",EDGE,"E33.3")])],"isStart":false});var subQ2=makeQuery(id+"F5.imprint","INTERSECT",VERTEX,{"derivedFrom":[subQ1,subQ0]});Q11=makeQuery(id+"F5.imprint","IMPRINT",FACE,{"disambiguationData":[TD([[makeQuery(id+"F5.imprint","IMPRINT",EDGE,{"disambiguationData":[TD([[subQ2,-1.0]])],"derivedFrom":subQ0}),1.0]])]});}
            var Q12;
            {var subQ0=sQuery(id+"F5.wireOp",EDGE,"E38.14.0.0");var subQ1=makeQuery(id+"F1.opExtrude","CAP_EDGE",EDGE,{"disambiguationData":[OSD([sQuery(id+"F0.wireOp",EDGE,"E33.2")])],"isStart":false});var subQ2=makeQuery(id+"F5.imprint","INTERSECT",VERTEX,{"derivedFrom":[subQ1,subQ0]});Q12=makeQuery(id+"F5.imprint","IMPRINT",FACE,{"disambiguationData":[TD([[makeQuery(id+"F5.imprint","IMPRINT",EDGE,{"disambiguationData":[TD([[subQ2,-1.0]])],"derivedFrom":subQ0}),1.0]])]});}
            var Q13;
            {var subQ0=sQuery(id+"F5.wireOp",EDGE,"E38.13.0.0");var subQ1=makeQuery(id+"F1.opExtrude","CAP_EDGE",EDGE,{"disambiguationData":[OSD([sQuery(id+"F0.wireOp",EDGE,"E33.2")])],"isStart":false});var subQ2=makeQuery(id+"F5.imprint","INTERSECT",VERTEX,{"derivedFrom":[subQ1,subQ0]});Q13=makeQuery(id+"F5.imprint","IMPRINT",FACE,{"disambiguationData":[TD([[makeQuery(id+"F5.imprint","IMPRINT",EDGE,{"disambiguationData":[TD([[subQ2,-1.0]])],"derivedFrom":subQ0}),1.0]])]});}
            var Q14;
            {var subQ0=sQuery(id+"F5.wireOp",EDGE,"E38.12.0.0");var subQ1=makeQuery(id+"F1.opExtrude","CAP_EDGE",EDGE,{"disambiguationData":[OSD([sQuery(id+"F0.wireOp",EDGE,"E33.2")])],"isStart":false});var subQ2=makeQuery(id+"F5.imprint","INTERSECT",VERTEX,{"derivedFrom":[subQ1,subQ0]});Q14=makeQuery(id+"F5.imprint","IMPRINT",FACE,{"disambiguationData":[TD([[makeQuery(id+"F5.imprint","IMPRINT",EDGE,{"disambiguationData":[TD([[subQ2,-1.0]])],"derivedFrom":subQ0}),1.0]])]});}
            var Q15;
            {var subQ0=sQuery(id+"F5.wireOp",EDGE,"E38.13.0.0");var subQ1=makeQuery(id+"F1.opExtrude","CAP_EDGE",EDGE,{"disambiguationData":[OSD([sQuery(id+"F0.wireOp",EDGE,"E33.6")])],"isStart":false});var subQ2=makeQuery(id+"F5.imprint","INTERSECT",VERTEX,{"derivedFrom":[subQ1,subQ0]});Q15=makeQuery(id+"F5.imprint","IMPRINT",FACE,{"disambiguationData":[TD([[makeQuery(id+"F5.imprint","IMPRINT",EDGE,{"disambiguationData":[TD([[subQ2,-1.0]])],"derivedFrom":subQ0}),1.0]])]});}
            var Q16;
            {var subQ0=sQuery(id+"F5.wireOp",EDGE,"E38.14.0.0");var subQ1=makeQuery(id+"F1.opExtrude","CAP_EDGE",EDGE,{"disambiguationData":[OSD([sQuery(id+"F0.wireOp",EDGE,"E33.6")])],"isStart":false});var subQ2=makeQuery(id+"F5.imprint","INTERSECT",VERTEX,{"derivedFrom":[subQ1,subQ0]});Q16=makeQuery(id+"F5.imprint","IMPRINT",FACE,{"disambiguationData":[TD([[makeQuery(id+"F5.imprint","IMPRINT",EDGE,{"disambiguationData":[TD([[subQ2,-1.0]])],"derivedFrom":subQ0}),1.0]])]});}
            var Q17;
            {var subQ0=sQuery(id+"F5.wireOp",EDGE,"E38.9.0.0");var subQ1=makeQuery(id+"F1.opExtrude","CAP_EDGE",EDGE,{"disambiguationData":[OSD([sQuery(id+"F0.wireOp",EDGE,"E33.13")])],"isStart":false});var subQ2=makeQuery(id+"F5.imprint","INTERSECT",VERTEX,{"derivedFrom":[subQ1,subQ0]});Q17=makeQuery(id+"F5.imprint","IMPRINT",FACE,{"disambiguationData":[TD([[makeQuery(id+"F5.imprint","IMPRINT",EDGE,{"disambiguationData":[TD([[subQ2,-1.0]])],"derivedFrom":subQ0}),1.0]])]});}
            var Q18;
            {var subQ0=sQuery(id+"F5.wireOp",EDGE,"E38.16.0.0");var subQ1=makeQuery(id+"F1.opExtrude","CAP_EDGE",EDGE,{"disambiguationData":[OSD([sQuery(id+"F0.wireOp",EDGE,"E33.6")])],"isStart":false});var subQ2=makeQuery(id+"F5.imprint","INTERSECT",VERTEX,{"derivedFrom":[subQ1,subQ0]});Q18=makeQuery(id+"F5.imprint","IMPRINT",FACE,{"disambiguationData":[TD([[makeQuery(id+"F5.imprint","IMPRINT",EDGE,{"disambiguationData":[TD([[subQ2,-1.0]])],"derivedFrom":subQ0}),1.0]])]});}
            var Q19;
            {var subQ0=sQuery(id+"F5.wireOp",EDGE,"E38.15.0.0");var subQ1=makeQuery(id+"F1.opExtrude","CAP_EDGE",EDGE,{"disambiguationData":[OSD([sQuery(id+"F0.wireOp",EDGE,"E33.6")])],"isStart":false});var subQ2=makeQuery(id+"F5.imprint","INTERSECT",VERTEX,{"derivedFrom":[subQ1,subQ0]});Q19=makeQuery(id+"F5.imprint","IMPRINT",FACE,{"disambiguationData":[TD([[makeQuery(id+"F5.imprint","IMPRINT",EDGE,{"disambiguationData":[TD([[subQ2,-1.0]])],"derivedFrom":subQ0}),1.0]])]});}
            var Q20;
            {var subQ0=sQuery(id+"F5.wireOp",EDGE,"E38.2.0.0");var subQ1=makeQuery(id+"F1.opExtrude","CAP_EDGE",EDGE,{"disambiguationData":[OSD([sQuery(id+"F0.wireOp",EDGE,"E33.12")])],"isStart":false});var subQ2=makeQuery(id+"F5.imprint","INTERSECT",VERTEX,{"derivedFrom":[subQ1,subQ0]});Q20=makeQuery(id+"F5.imprint","IMPRINT",FACE,{"disambiguationData":[TD([[makeQuery(id+"F5.imprint","IMPRINT",EDGE,{"disambiguationData":[TD([[subQ2,-1.0]])],"derivedFrom":subQ0}),1.0]])]});}
            var Q21;
            {var subQ0=sQuery(id+"F5.wireOp",EDGE,"E38.3.0.0");var subQ1=makeQuery(id+"F1.opExtrude","CAP_EDGE",EDGE,{"disambiguationData":[OSD([sQuery(id+"F0.wireOp",EDGE,"E33.12")])],"isStart":false});var subQ2=makeQuery(id+"F5.imprint","INTERSECT",VERTEX,{"derivedFrom":[subQ1,subQ0]});Q21=makeQuery(id+"F5.imprint","IMPRINT",FACE,{"disambiguationData":[TD([[makeQuery(id+"F5.imprint","IMPRINT",EDGE,{"disambiguationData":[TD([[subQ2,-1.0]])],"derivedFrom":subQ0}),1.0]])]});}
            var Q22;
            {var subQ0=sQuery(id+"F5.wireOp",EDGE,"E38.4.0.0");var subQ1=makeQuery(id+"F1.opExtrude","CAP_EDGE",EDGE,{"disambiguationData":[OSD([sQuery(id+"F0.wireOp",EDGE,"E33.12")])],"isStart":false});var subQ2=makeQuery(id+"F5.imprint","INTERSECT",VERTEX,{"derivedFrom":[subQ1,subQ0]});Q22=makeQuery(id+"F5.imprint","IMPRINT",FACE,{"disambiguationData":[TD([[makeQuery(id+"F5.imprint","IMPRINT",EDGE,{"disambiguationData":[TD([[subQ2,-1.0]])],"derivedFrom":subQ0}),1.0]])]});}
            var Q23;
            {var subQ0=sQuery(id+"F5.wireOp",EDGE,"E38.5.0.0");var subQ1=makeQuery(id+"F1.opExtrude","CAP_EDGE",EDGE,{"disambiguationData":[OSD([sQuery(id+"F0.wireOp",EDGE,"E33.12")])],"isStart":false});var subQ2=makeQuery(id+"F5.imprint","INTERSECT",VERTEX,{"derivedFrom":[subQ1,subQ0]});Q23=makeQuery(id+"F5.imprint","IMPRINT",FACE,{"disambiguationData":[TD([[makeQuery(id+"F5.imprint","IMPRINT",EDGE,{"disambiguationData":[TD([[subQ2,-1.0]])],"derivedFrom":subQ0}),1.0]])]});}
            var Q24;
            {var subQ0=sQuery(id+"F5.wireOp",EDGE,"E38.6.0.0");var subQ1=makeQuery(id+"F1.opExtrude","CAP_EDGE",EDGE,{"disambiguationData":[OSD([sQuery(id+"F0.wireOp",EDGE,"E33.12")])],"isStart":false});var subQ2=makeQuery(id+"F5.imprint","INTERSECT",VERTEX,{"derivedFrom":[subQ1,subQ0]});Q24=makeQuery(id+"F5.imprint","IMPRINT",FACE,{"disambiguationData":[TD([[makeQuery(id+"F5.imprint","IMPRINT",EDGE,{"disambiguationData":[TD([[subQ2,-1.0]])],"derivedFrom":subQ0}),1.0]])]});}
            var Q25;
            {var subQ0=sQuery(id+"F5.wireOp",EDGE,"E38.7.0.0");var subQ1=makeQuery(id+"F1.opExtrude","CAP_EDGE",EDGE,{"disambiguationData":[OSD([sQuery(id+"F0.wireOp",EDGE,"E33.12")])],"isStart":false});var subQ2=makeQuery(id+"F5.imprint","INTERSECT",VERTEX,{"derivedFrom":[subQ1,subQ0]});Q25=makeQuery(id+"F5.imprint","IMPRINT",FACE,{"disambiguationData":[TD([[makeQuery(id+"F5.imprint","IMPRINT",EDGE,{"disambiguationData":[TD([[subQ2,-1.0]])],"derivedFrom":subQ0}),1.0]])]});}
            var Q26;
            {var subQ0=sQuery(id+"F5.wireOp",EDGE,"E38.8.0.0");var subQ1=makeQuery(id+"F1.opExtrude","CAP_EDGE",EDGE,{"disambiguationData":[OSD([sQuery(id+"F0.wireOp",EDGE,"E33.12")])],"isStart":false});var subQ2=makeQuery(id+"F5.imprint","INTERSECT",VERTEX,{"derivedFrom":[subQ1,subQ0]});Q26=makeQuery(id+"F5.imprint","IMPRINT",FACE,{"disambiguationData":[TD([[makeQuery(id+"F5.imprint","IMPRINT",EDGE,{"disambiguationData":[TD([[subQ2,-1.0]])],"derivedFrom":subQ0}),1.0]])]});}
            var Q27;
            {var subQ0=sQuery(id+"F5.wireOp",EDGE,"E38.13.0.0");var subQ1=makeQuery(id+"F1.opExtrude","CAP_EDGE",EDGE,{"disambiguationData":[OSD([sQuery(id+"F0.wireOp",EDGE,"E33.20")])],"isStart":false});var subQ2=makeQuery(id+"F5.imprint","INTERSECT",VERTEX,{"derivedFrom":[subQ1,subQ0]});Q27=makeQuery(id+"F5.imprint","IMPRINT",FACE,{"disambiguationData":[TD([[makeQuery(id+"F5.imprint","IMPRINT",EDGE,{"disambiguationData":[TD([[subQ2,-1.0]])],"derivedFrom":subQ0}),1.0]])]});}
            var Q28;
            {var subQ0=sQuery(id+"F5.wireOp",EDGE,"E38.14.0.0");var subQ1=makeQuery(id+"F1.opExtrude","CAP_EDGE",EDGE,{"disambiguationData":[OSD([sQuery(id+"F0.wireOp",EDGE,"E33.20")])],"isStart":false});var subQ2=makeQuery(id+"F5.imprint","INTERSECT",VERTEX,{"derivedFrom":[subQ1,subQ0]});Q28=makeQuery(id+"F5.imprint","IMPRINT",FACE,{"disambiguationData":[TD([[makeQuery(id+"F5.imprint","IMPRINT",EDGE,{"disambiguationData":[TD([[subQ2,-1.0]])],"derivedFrom":subQ1}),-1.0]])]});}
            var Q29;
            {var subQ0=sQuery(id+"F5.wireOp",EDGE,"E38.15.0.0");var subQ1=makeQuery(id+"F1.opExtrude","CAP_EDGE",EDGE,{"disambiguationData":[OSD([sQuery(id+"F0.wireOp",EDGE,"E33.20")])],"isStart":false});var subQ2=makeQuery(id+"F5.imprint","INTERSECT",VERTEX,{"derivedFrom":[subQ1,subQ0]});Q29=makeQuery(id+"F5.imprint","IMPRINT",FACE,{"disambiguationData":[TD([[makeQuery(id+"F5.imprint","IMPRINT",EDGE,{"disambiguationData":[TD([[subQ2,-1.0]])],"derivedFrom":subQ1}),-1.0]])]});}
            var Q30;
            {var subQ0=sQuery(id+"F5.wireOp",EDGE,"E38.12.0.0");var subQ1=makeQuery(id+"F1.opExtrude","CAP_EDGE",EDGE,{"disambiguationData":[OSD([sQuery(id+"F0.wireOp",EDGE,"E33.20")])],"isStart":false});var subQ2=makeQuery(id+"F5.imprint","INTERSECT",VERTEX,{"derivedFrom":[subQ1,subQ0]});Q30=makeQuery(id+"F5.imprint","IMPRINT",FACE,{"disambiguationData":[TD([[makeQuery(id+"F5.imprint","IMPRINT",EDGE,{"disambiguationData":[TD([[subQ2,-1.0]])],"derivedFrom":subQ0}),1.0]])]});}
            var Q31;
            {var subQ0=sQuery(id+"F5.wireOp",EDGE,"E38.11.0.0");var subQ1=makeQuery(id+"F1.opExtrude","CAP_EDGE",EDGE,{"disambiguationData":[OSD([sQuery(id+"F0.wireOp",EDGE,"E33.20")])],"isStart":false});var subQ2=makeQuery(id+"F5.imprint","INTERSECT",VERTEX,{"derivedFrom":[subQ1,subQ0]});Q31=makeQuery(id+"F5.imprint","IMPRINT",FACE,{"disambiguationData":[TD([[makeQuery(id+"F5.imprint","IMPRINT",EDGE,{"disambiguationData":[TD([[subQ2,-1.0]])],"derivedFrom":subQ0}),1.0]])]});}
            var Q32;
            {var subQ0=sQuery(id+"F5.wireOp",EDGE,"E38.16.0.0");var subQ1=makeQuery(id+"F1.opExtrude","CAP_EDGE",EDGE,{"disambiguationData":[OSD([sQuery(id+"F0.wireOp",EDGE,"E33.20")])],"isStart":false});var subQ2=makeQuery(id+"F5.imprint","INTERSECT",VERTEX,{"derivedFrom":[subQ1,subQ0]});Q32=makeQuery(id+"F5.imprint","IMPRINT",FACE,{"disambiguationData":[TD([[makeQuery(id+"F5.imprint","IMPRINT",EDGE,{"disambiguationData":[TD([[subQ2,-1.0]])],"derivedFrom":subQ1}),-1.0]])]});}
            var Q33;
            {var subQ0=sQuery(id+"F5.wireOp",EDGE,"E38.17.0.0");var subQ1=makeQuery(id+"F1.opExtrude","CAP_EDGE",EDGE,{"disambiguationData":[OSD([sQuery(id+"F0.wireOp",EDGE,"E33.20")])],"isStart":false});var subQ2=makeQuery(id+"F5.imprint","INTERSECT",VERTEX,{"derivedFrom":[subQ1,subQ0]});Q33=makeQuery(id+"F5.imprint","IMPRINT",FACE,{"disambiguationData":[TD([[makeQuery(id+"F5.imprint","IMPRINT",EDGE,{"disambiguationData":[TD([[subQ2,-1.0]])],"derivedFrom":subQ1}),-1.0]])]});}
            var Q34;
            {var subQ0=sQuery(id+"F5.wireOp",EDGE,"E38.17.0.0");var subQ1=makeQuery(id+"F1.opExtrude","CAP_EDGE",EDGE,{"disambiguationData":[OSD([sQuery(id+"F0.wireOp",EDGE,"E33.6")])],"isStart":false});var subQ2=makeQuery(id+"F5.imprint","INTERSECT",VERTEX,{"derivedFrom":[subQ1,subQ0]});Q34=makeQuery(id+"F5.imprint","IMPRINT",FACE,{"disambiguationData":[TD([[makeQuery(id+"F5.imprint","IMPRINT",EDGE,{"disambiguationData":[TD([[subQ2,-1.0]])],"derivedFrom":subQ0}),1.0]])]});}
            var Q35;
            {var subQ0=sQuery(id+"F5.wireOp",EDGE,"E38.18.0.0");var subQ1=makeQuery(id+"F1.opExtrude","CAP_EDGE",EDGE,{"disambiguationData":[OSD([sQuery(id+"F0.wireOp",EDGE,"E33.6")])],"isStart":false});var subQ2=makeQuery(id+"F5.imprint","INTERSECT",VERTEX,{"derivedFrom":[subQ1,subQ0]});Q35=makeQuery(id+"F5.imprint","IMPRINT",FACE,{"disambiguationData":[TD([[makeQuery(id+"F5.imprint","IMPRINT",EDGE,{"disambiguationData":[TD([[subQ2,-1.0]])],"derivedFrom":subQ1}),-1.0]])]});}
            var Q36;
            {var subQ0=sQuery(id+"F5.wireOp",EDGE,"E38.19.0.0");var subQ1=makeQuery(id+"F1.opExtrude","CAP_EDGE",EDGE,{"disambiguationData":[OSD([sQuery(id+"F0.wireOp",EDGE,"E33.6")])],"isStart":false});var subQ2=makeQuery(id+"F5.imprint","INTERSECT",VERTEX,{"derivedFrom":[subQ1,subQ0]});Q36=makeQuery(id+"F5.imprint","IMPRINT",FACE,{"disambiguationData":[TD([[makeQuery(id+"F5.imprint","IMPRINT",EDGE,{"disambiguationData":[TD([[subQ2,-1.0]])],"derivedFrom":subQ1}),-1.0]])]});}
            var Q37;
            {var subQ0=sQuery(id+"F5.wireOp",EDGE,"E39.0.20.0");var subQ1=makeQuery(id+"F1.opExtrude","CAP_EDGE",EDGE,{"disambiguationData":[OSD([sQuery(id+"F0.wireOp",EDGE,"E33.7")])],"isStart":false});var subQ2=makeQuery(id+"F5.imprint","INTERSECT",VERTEX,{"derivedFrom":[subQ1,subQ0]});Q37=makeQuery(id+"F5.imprint","IMPRINT",FACE,{"disambiguationData":[TD([[makeQuery(id+"F5.imprint","IMPRINT",EDGE,{"disambiguationData":[TD([[subQ2,-1.0]])],"derivedFrom":subQ1}),-1.0]])]});}
            var Q38;
            {var subQ0=sQuery(id+"F5.wireOp",EDGE,"E38.1.0.1");var subQ1=makeQuery(id+"F1.opExtrude","CAP_EDGE",EDGE,{"disambiguationData":[OSD([sQuery(id+"F0.wireOp",EDGE,"E33.17")])],"isStart":false});var subQ2=makeQuery(id+"F5.imprint","INTERSECT",VERTEX,{"derivedFrom":[subQ1,subQ0]});Q38=makeQuery(id+"F5.imprint","IMPRINT",FACE,{"disambiguationData":[TD([[makeQuery(id+"F5.imprint","IMPRINT",EDGE,{"disambiguationData":[TD([[subQ2,-1.0]])],"derivedFrom":subQ0}),1.0]])]});}
            var Q39;
            {var subQ0=sQuery(id+"F5.wireOp",EDGE,"E38.10.0.1");var subQ1=makeQuery(id+"F1.opExtrude","CAP_EDGE",EDGE,{"disambiguationData":[OSD([sQuery(id+"F0.wireOp",EDGE,"E33.21")])],"isStart":false});var subQ2=makeQuery(id+"F5.imprint","INTERSECT",VERTEX,{"derivedFrom":[subQ1,subQ0]});Q39=makeQuery(id+"F5.imprint","IMPRINT",FACE,{"disambiguationData":[TD([[makeQuery(id+"F5.imprint","IMPRINT",EDGE,{"disambiguationData":[TD([[subQ2,-1.0]])],"derivedFrom":subQ0}),1.0]])]});}
            var Q40;
            {var subQ0=sQuery(id+"F5.wireOp",EDGE,"E38.3.0.0");var subQ1=makeQuery(id+"F1.opExtrude","CAP_EDGE",EDGE,{"disambiguationData":[OSD([sQuery(id+"F0.wireOp",EDGE,"E33.12")])],"isStart":false});var subQ2=makeQuery(id+"F5.imprint","INTERSECT",VERTEX,{"derivedFrom":[subQ1,subQ0]});Q40=makeQuery(id+"F5.imprint","IMPRINT",FACE,{"disambiguationData":[TD([[makeQuery(id+"F5.imprint","IMPRINT",EDGE,{"disambiguationData":[TD([[subQ2,-1.0]])],"derivedFrom":subQ0}),1.0]])]});}
            var Q41;
            {var subQ0=sQuery(id+"F5.wireOp",EDGE,"E38.11.0.0");var subQ1=sQuery(id+"F0.wireOp",EDGE,"E33.1");var subQ5=makeQuery(id+"F1.opExtrude","CAP_EDGE",EDGE,{"disambiguationData":[OSD([subQ1])],"isStart":false});var subQ6=makeQuery(id+"F5.imprint","INTERSECT",VERTEX,{"derivedFrom":[subQ5,subQ0]});Q41=makeQuery(id+"F5.imprint","IMPRINT",FACE,{"disambiguationData":[TD([[makeQuery(id+"F5.imprint","IMPRINT",EDGE,{"disambiguationData":[TD([[subQ6,-1.0]])],"derivedFrom":subQ5}),1.0]])]});}
            extrude(context, id + "F7", {"entities" : qUnion([Q0, Q1, Q2, Q3, Q4, Q5, Q6, Q7, Q8, Q9, Q10, Q11, Q12, Q13, Q14, Q15, Q16, Q17, Q18, Q19, Q20, Q21, Q22, Q23, Q24, Q25, Q26, Q27, Q28, Q29, Q30, Q31, Q32, Q33, Q34, Q35, Q36, Q37, Q38, Q39, Q40, Q41]), "operationType" : NewBodyOperationType.ADD, "oppositeDirection" : true, "depth" : 2 * mm, "offsetDistance" : 25 * mm});
        }
        {
            var Q0;
            {var subQ0=sQuery(id+"F6.wireOp",EDGE,"E43.18.0.0");var subQ1=makeQuery(id+"F1.opExtrude","CAP_EDGE",EDGE,{"disambiguationData":[OSD([sQuery(id+"F0.wireOp",EDGE,"E33.5")])],"isStart":false});var subQ2=makeQuery(id+"F6.imprint","INTERSECT",VERTEX,{"derivedFrom":[subQ1,subQ0]});Q0=makeQuery(id+"F6.imprint","IMPRINT",FACE,{"disambiguationData":[TD([[makeQuery(id+"F6.imprint","IMPRINT",EDGE,{"disambiguationData":[TD([[subQ2,-1.0]])],"derivedFrom":subQ0}),-1.0]])]});}
            var Q1;
            {var subQ2=sQuery(id+"F0.wireOp",EDGE,"E33.5");var subQ8=sQuery(id+"F6.wireOp",EDGE,"E43.19.0.1");var subQ10=makeQuery(id+"F1.opExtrude","CAP_EDGE",EDGE,{"disambiguationData":[OSD([subQ2])],"isStart":false});var subQ11=makeQuery(id+"F6.imprint","INTERSECT",VERTEX,{"derivedFrom":[subQ10,subQ8]});Q1=makeQuery(id+"F6.imprint","IMPRINT",FACE,{"disambiguationData":[TD([[makeQuery(id+"F6.imprint","IMPRINT",EDGE,{"disambiguationData":[TD([[subQ11,-1.0]])],"derivedFrom":subQ8}),1.0]])]});}
            var Q2;
            {var subQ0=sQuery(id+"F6.wireOp",EDGE,"E43.17.0.0");var subQ1=makeQuery(id+"F1.opExtrude","CAP_EDGE",EDGE,{"disambiguationData":[OSD([sQuery(id+"F0.wireOp",EDGE,"E33.13")])],"isStart":false});var subQ2=makeQuery(id+"F6.imprint","INTERSECT",VERTEX,{"derivedFrom":[subQ1,subQ0]});Q2=makeQuery(id+"F6.imprint","IMPRINT",FACE,{"disambiguationData":[TD([[makeQuery(id+"F6.imprint","IMPRINT",EDGE,{"disambiguationData":[TD([[subQ2,-1.0]])],"derivedFrom":subQ0}),-1.0]])]});}
            var Q3;
            {var subQ0=sQuery(id+"F6.wireOp",EDGE,"E43.17.0.0");var subQ1=makeQuery(id+"F1.opExtrude","CAP_EDGE",EDGE,{"disambiguationData":[OSD([sQuery(id+"F0.wireOp",EDGE,"E33.5")])],"isStart":false});var subQ2=makeQuery(id+"F6.imprint","INTERSECT",VERTEX,{"derivedFrom":[subQ1,subQ0]});Q3=makeQuery(id+"F6.imprint","IMPRINT",FACE,{"disambiguationData":[TD([[makeQuery(id+"F6.imprint","IMPRINT",EDGE,{"disambiguationData":[TD([[subQ2,-1.0]])],"derivedFrom":subQ0}),-1.0]])]});}
            var Q4;
            {var subQ0=sQuery(id+"F6.wireOp",EDGE,"E43.16.0.0");var subQ1=makeQuery(id+"F1.opExtrude","CAP_EDGE",EDGE,{"disambiguationData":[OSD([sQuery(id+"F0.wireOp",EDGE,"E33.5")])],"isStart":false});var subQ2=makeQuery(id+"F6.imprint","INTERSECT",VERTEX,{"derivedFrom":[subQ1,subQ0]});Q4=makeQuery(id+"F6.imprint","IMPRINT",FACE,{"disambiguationData":[TD([[makeQuery(id+"F6.imprint","IMPRINT",EDGE,{"disambiguationData":[TD([[subQ2,-1.0]])],"derivedFrom":subQ0}),-1.0]])]});}
            var Q5;
            {var subQ0=sQuery(id+"F6.wireOp",EDGE,"E43.15.0.0");var subQ1=makeQuery(id+"F1.opExtrude","CAP_EDGE",EDGE,{"disambiguationData":[OSD([sQuery(id+"F0.wireOp",EDGE,"E33.5")])],"isStart":false});var subQ2=makeQuery(id+"F6.imprint","INTERSECT",VERTEX,{"derivedFrom":[subQ1,subQ0]});Q5=makeQuery(id+"F6.imprint","IMPRINT",FACE,{"disambiguationData":[TD([[makeQuery(id+"F6.imprint","IMPRINT",EDGE,{"disambiguationData":[TD([[subQ2,-1.0]])],"derivedFrom":subQ0}),-1.0]])]});}
            var Q6;
            {var subQ0=sQuery(id+"F6.wireOp",EDGE,"E43.14.0.0");var subQ1=makeQuery(id+"F1.opExtrude","CAP_EDGE",EDGE,{"disambiguationData":[OSD([sQuery(id+"F0.wireOp",EDGE,"E33.5")])],"isStart":false});var subQ2=makeQuery(id+"F6.imprint","INTERSECT",VERTEX,{"derivedFrom":[subQ1,subQ0]});Q6=makeQuery(id+"F6.imprint","IMPRINT",FACE,{"disambiguationData":[TD([[makeQuery(id+"F6.imprint","IMPRINT",EDGE,{"disambiguationData":[TD([[subQ2,-1.0]])],"derivedFrom":subQ0}),-1.0]])]});}
            var Q7;
            {var subQ0=sQuery(id+"F6.wireOp",EDGE,"E43.13.0.0");var subQ1=makeQuery(id+"F1.opExtrude","CAP_EDGE",EDGE,{"disambiguationData":[OSD([sQuery(id+"F0.wireOp",EDGE,"E33.15")])],"isStart":false});var subQ2=makeQuery(id+"F6.imprint","INTERSECT",VERTEX,{"derivedFrom":[subQ1,subQ0]});Q7=makeQuery(id+"F6.imprint","IMPRINT",FACE,{"disambiguationData":[TD([[makeQuery(id+"F6.imprint","IMPRINT",EDGE,{"disambiguationData":[TD([[subQ2,-1.0]])],"derivedFrom":subQ0}),-1.0]])]});}
            var Q8;
            {var subQ0=sQuery(id+"F6.wireOp",EDGE,"E43.12.0.0");var subQ1=makeQuery(id+"F1.opExtrude","CAP_EDGE",EDGE,{"disambiguationData":[OSD([sQuery(id+"F0.wireOp",EDGE,"E33.15")])],"isStart":false});var subQ2=makeQuery(id+"F6.imprint","INTERSECT",VERTEX,{"derivedFrom":[subQ1,subQ0]});Q8=makeQuery(id+"F6.imprint","IMPRINT",FACE,{"disambiguationData":[TD([[makeQuery(id+"F6.imprint","IMPRINT",EDGE,{"disambiguationData":[TD([[subQ2,-1.0]])],"derivedFrom":subQ0}),-1.0]])]});}
            var Q9;
            {var subQ0=sQuery(id+"F6.wireOp",EDGE,"E43.16.0.0");var subQ1=makeQuery(id+"F1.opExtrude","CAP_EDGE",EDGE,{"disambiguationData":[OSD([sQuery(id+"F0.wireOp",EDGE,"E33.13")])],"isStart":false});var subQ2=makeQuery(id+"F6.imprint","INTERSECT",VERTEX,{"derivedFrom":[subQ1,subQ0]});Q9=makeQuery(id+"F6.imprint","IMPRINT",FACE,{"disambiguationData":[TD([[makeQuery(id+"F6.imprint","IMPRINT",EDGE,{"disambiguationData":[TD([[subQ2,-1.0]])],"derivedFrom":subQ0}),-1.0]])]});}
            var Q10;
            {var subQ0=sQuery(id+"F6.wireOp",EDGE,"E43.15.0.0");var subQ1=makeQuery(id+"F1.opExtrude","CAP_EDGE",EDGE,{"disambiguationData":[OSD([sQuery(id+"F0.wireOp",EDGE,"E33.13")])],"isStart":false});var subQ2=makeQuery(id+"F6.imprint","INTERSECT",VERTEX,{"derivedFrom":[subQ1,subQ0]});Q10=makeQuery(id+"F6.imprint","IMPRINT",FACE,{"disambiguationData":[TD([[makeQuery(id+"F6.imprint","IMPRINT",EDGE,{"disambiguationData":[TD([[subQ2,-1.0]])],"derivedFrom":subQ0}),-1.0]])]});}
            var Q11;
            {var subQ0=sQuery(id+"F6.wireOp",EDGE,"E43.14.0.0");var subQ1=makeQuery(id+"F1.opExtrude","CAP_EDGE",EDGE,{"disambiguationData":[OSD([sQuery(id+"F0.wireOp",EDGE,"E33.13")])],"isStart":false});var subQ2=makeQuery(id+"F6.imprint","INTERSECT",VERTEX,{"derivedFrom":[subQ1,subQ0]});Q11=makeQuery(id+"F6.imprint","IMPRINT",FACE,{"disambiguationData":[TD([[makeQuery(id+"F6.imprint","IMPRINT",EDGE,{"disambiguationData":[TD([[subQ2,-1.0]])],"derivedFrom":subQ0}),-1.0]])]});}
            var Q12;
            {var subQ0=sQuery(id+"F6.wireOp",EDGE,"E43.13.0.0");var subQ1=makeQuery(id+"F1.opExtrude","CAP_EDGE",EDGE,{"disambiguationData":[OSD([sQuery(id+"F0.wireOp",EDGE,"E33.13")])],"isStart":false});var subQ2=makeQuery(id+"F6.imprint","INTERSECT",VERTEX,{"derivedFrom":[subQ1,subQ0]});Q12=makeQuery(id+"F6.imprint","IMPRINT",FACE,{"disambiguationData":[TD([[makeQuery(id+"F6.imprint","IMPRINT",EDGE,{"disambiguationData":[TD([[subQ2,-1.0]])],"derivedFrom":subQ0}),-1.0]])]});}
            var Q13;
            {var subQ0=sQuery(id+"F6.wireOp",EDGE,"E43.12.0.0");var subQ1=makeQuery(id+"F1.opExtrude","CAP_EDGE",EDGE,{"disambiguationData":[OSD([sQuery(id+"F0.wireOp",EDGE,"E33.13")])],"isStart":false});var subQ2=makeQuery(id+"F6.imprint","INTERSECT",VERTEX,{"derivedFrom":[subQ1,subQ0]});Q13=makeQuery(id+"F6.imprint","IMPRINT",FACE,{"disambiguationData":[TD([[makeQuery(id+"F6.imprint","IMPRINT",EDGE,{"disambiguationData":[TD([[subQ2,-1.0]])],"derivedFrom":subQ0}),-1.0]])]});}
            var Q14;
            {var subQ0=sQuery(id+"F6.wireOp",EDGE,"E43.13.0.0");var subQ1=makeQuery(id+"F1.opExtrude","CAP_EDGE",EDGE,{"disambiguationData":[OSD([sQuery(id+"F0.wireOp",EDGE,"E33.2")])],"isStart":false});var subQ2=makeQuery(id+"F6.imprint","INTERSECT",VERTEX,{"derivedFrom":[subQ1,subQ0]});Q14=makeQuery(id+"F6.imprint","IMPRINT",FACE,{"disambiguationData":[TD([[makeQuery(id+"F6.imprint","IMPRINT",EDGE,{"disambiguationData":[TD([[subQ2,-1.0]])],"derivedFrom":subQ0}),-1.0]])]});}
            var Q15;
            {var subQ0=sQuery(id+"F6.wireOp",EDGE,"E43.14.0.0");var subQ1=makeQuery(id+"F1.opExtrude","CAP_EDGE",EDGE,{"disambiguationData":[OSD([sQuery(id+"F0.wireOp",EDGE,"E33.2")])],"isStart":false});var subQ2=makeQuery(id+"F6.imprint","INTERSECT",VERTEX,{"derivedFrom":[subQ1,subQ0]});Q15=makeQuery(id+"F6.imprint","IMPRINT",FACE,{"disambiguationData":[TD([[makeQuery(id+"F6.imprint","IMPRINT",EDGE,{"disambiguationData":[TD([[subQ2,-1.0]])],"derivedFrom":subQ0}),-1.0]])]});}
            var Q16;
            {var subQ0=sQuery(id+"F6.wireOp",EDGE,"E43.15.0.0");var subQ1=makeQuery(id+"F1.opExtrude","CAP_EDGE",EDGE,{"disambiguationData":[OSD([sQuery(id+"F0.wireOp",EDGE,"E33.2")])],"isStart":false});var subQ2=makeQuery(id+"F6.imprint","INTERSECT",VERTEX,{"derivedFrom":[subQ1,subQ0]});Q16=makeQuery(id+"F6.imprint","IMPRINT",FACE,{"disambiguationData":[TD([[makeQuery(id+"F6.imprint","IMPRINT",EDGE,{"disambiguationData":[TD([[subQ2,-1.0]])],"derivedFrom":subQ0}),-1.0]])]});}
            var Q17;
            {var subQ5=sQuery(id+"F6.wireOp",EDGE,"E43.16.0.0");var subQ7=makeQuery(id+"F1.opExtrude","CAP_EDGE",EDGE,{"disambiguationData":[OSD([sQuery(id+"F0.wireOp",EDGE,"E33.2")])],"isStart":false});var subQ9=makeQuery(id+"F6.imprint","INTERSECT",VERTEX,{"derivedFrom":[subQ7,subQ5]});Q17=makeQuery(id+"F6.imprint","IMPRINT",FACE,{"disambiguationData":[TD([[makeQuery(id+"F6.imprint","IMPRINT",EDGE,{"disambiguationData":[TD([[subQ9,-1.0]])],"derivedFrom":subQ5}),-1.0]])]});}
            var Q18;
            {var subQ0=sQuery(id+"F6.wireOp",EDGE,"E43.17.0.1");var subQ1=makeQuery(id+"F1.opExtrude","CAP_EDGE",EDGE,{"disambiguationData":[OSD([sQuery(id+"F0.wireOp",EDGE,"E33.2")])],"isStart":false});var subQ2=makeQuery(id+"F6.imprint","INTERSECT",VERTEX,{"derivedFrom":[subQ1,subQ0]});Q18=makeQuery(id+"F6.imprint","IMPRINT",FACE,{"disambiguationData":[TD([[makeQuery(id+"F6.imprint","IMPRINT",EDGE,{"disambiguationData":[TD([[subQ2,-1.0]])],"derivedFrom":subQ0}),1.0]])]});}
            var Q19;
            {var subQ3=sQuery(id+"F6.wireOp",EDGE,"E43.11.0.1");var subQ9=makeQuery(id+"F1.opExtrude","CAP_EDGE",EDGE,{"disambiguationData":[OSD([sQuery(id+"F0.wireOp",EDGE,"E33.13")])],"isStart":false});var subQ11=makeQuery(id+"F6.imprint","INTERSECT",VERTEX,{"derivedFrom":[subQ9,subQ3]});Q19=makeQuery(id+"F6.imprint","IMPRINT",FACE,{"disambiguationData":[TD([[makeQuery(id+"F6.imprint","IMPRINT",EDGE,{"disambiguationData":[TD([[subQ11,-1.0]])],"derivedFrom":subQ3}),1.0]])]});}
            var Q20;
            {var subQ0=sQuery(id+"F6.wireOp",EDGE,"E43.10.0.0");var subQ1=makeQuery(id+"F1.opExtrude","CAP_EDGE",EDGE,{"disambiguationData":[OSD([sQuery(id+"F0.wireOp",EDGE,"E33.12")])],"isStart":false});var subQ2=makeQuery(id+"F6.imprint","INTERSECT",VERTEX,{"derivedFrom":[subQ1,subQ0]});Q20=makeQuery(id+"F6.imprint","IMPRINT",FACE,{"disambiguationData":[TD([[makeQuery(id+"F6.imprint","IMPRINT",EDGE,{"disambiguationData":[TD([[subQ2,-1.0]])],"derivedFrom":subQ0}),-1.0]])]});}
            var Q21;
            {var subQ3=sQuery(id+"F6.wireOp",EDGE,"E43.9.0.0");var subQ6=makeQuery(id+"F1.opExtrude","CAP_EDGE",EDGE,{"disambiguationData":[OSD([sQuery(id+"F0.wireOp",EDGE,"E33.12")])],"isStart":false});var subQ9=makeQuery(id+"F6.imprint","INTERSECT",VERTEX,{"derivedFrom":[subQ6,subQ3]});Q21=makeQuery(id+"F6.imprint","IMPRINT",FACE,{"disambiguationData":[TD([[makeQuery(id+"F6.imprint","IMPRINT",EDGE,{"disambiguationData":[TD([[subQ9,-1.0]])],"derivedFrom":subQ3}),-1.0]])]});}
            var Q22;
            {var subQ5=sQuery(id+"F6.wireOp",EDGE,"E43.12.0.0");var subQ6=makeQuery(id+"F1.opExtrude","CAP_EDGE",EDGE,{"disambiguationData":[OSD([sQuery(id+"F0.wireOp",EDGE,"E33.6")])],"isStart":false});var subQ7=makeQuery(id+"F6.imprint","INTERSECT",VERTEX,{"derivedFrom":[subQ6,subQ5]});Q22=makeQuery(id+"F6.imprint","IMPRINT",FACE,{"disambiguationData":[TD([[makeQuery(id+"F6.imprint","IMPRINT",EDGE,{"disambiguationData":[TD([[subQ7,-1.0]])],"derivedFrom":subQ5}),-1.0]])]});}
            var Q23;
            {var subQ0=sQuery(id+"F6.wireOp",EDGE,"E43.8.0.0");var subQ1=makeQuery(id+"F1.opExtrude","CAP_EDGE",EDGE,{"disambiguationData":[OSD([sQuery(id+"F0.wireOp",EDGE,"E33.12")])],"isStart":false});var subQ2=makeQuery(id+"F6.imprint","INTERSECT",VERTEX,{"derivedFrom":[subQ1,subQ0]});Q23=makeQuery(id+"F6.imprint","IMPRINT",FACE,{"disambiguationData":[TD([[makeQuery(id+"F6.imprint","IMPRINT",EDGE,{"disambiguationData":[TD([[subQ2,-1.0]])],"derivedFrom":subQ0}),-1.0]])]});}
            var Q24;
            {var subQ0=sQuery(id+"F6.wireOp",EDGE,"E43.10.0.0");var subQ1=makeQuery(id+"F1.opExtrude","CAP_EDGE",EDGE,{"disambiguationData":[OSD([sQuery(id+"F0.wireOp",EDGE,"E33.20")])],"isStart":false});var subQ2=makeQuery(id+"F6.imprint","INTERSECT",VERTEX,{"derivedFrom":[subQ1,subQ0]});Q24=makeQuery(id+"F6.imprint","IMPRINT",FACE,{"disambiguationData":[TD([[makeQuery(id+"F6.imprint","IMPRINT",EDGE,{"disambiguationData":[TD([[subQ2,1.0]])],"derivedFrom":subQ1}),-1.0]])]});}
            var Q25;
            {var subQ0=sQuery(id+"F6.wireOp",EDGE,"E43.9.0.0");var subQ1=makeQuery(id+"F1.opExtrude","CAP_EDGE",EDGE,{"disambiguationData":[OSD([sQuery(id+"F0.wireOp",EDGE,"E33.20")])],"isStart":false});var subQ2=makeQuery(id+"F6.imprint","INTERSECT",VERTEX,{"derivedFrom":[subQ1,subQ0]});Q25=makeQuery(id+"F6.imprint","IMPRINT",FACE,{"disambiguationData":[TD([[makeQuery(id+"F6.imprint","IMPRINT",EDGE,{"disambiguationData":[TD([[subQ2,1.0]])],"derivedFrom":subQ1}),-1.0]])]});}
            var Q26;
            {var subQ0=sQuery(id+"F6.wireOp",EDGE,"E43.8.0.0");var subQ1=makeQuery(id+"F1.opExtrude","CAP_EDGE",EDGE,{"disambiguationData":[OSD([sQuery(id+"F0.wireOp",EDGE,"E33.20")])],"isStart":false});var subQ2=makeQuery(id+"F6.imprint","INTERSECT",VERTEX,{"derivedFrom":[subQ1,subQ0]});Q26=makeQuery(id+"F6.imprint","IMPRINT",FACE,{"disambiguationData":[TD([[makeQuery(id+"F6.imprint","IMPRINT",EDGE,{"disambiguationData":[TD([[subQ2,1.0]])],"derivedFrom":subQ1}),-1.0]])]});}
            var Q27;
            {var subQ0=sQuery(id+"F6.wireOp",EDGE,"E43.7.0.0");var subQ1=makeQuery(id+"F1.opExtrude","CAP_EDGE",EDGE,{"disambiguationData":[OSD([sQuery(id+"F0.wireOp",EDGE,"E33.20")])],"isStart":false});var subQ2=makeQuery(id+"F6.imprint","INTERSECT",VERTEX,{"derivedFrom":[subQ1,subQ0]});Q27=makeQuery(id+"F6.imprint","IMPRINT",FACE,{"disambiguationData":[TD([[makeQuery(id+"F6.imprint","IMPRINT",EDGE,{"disambiguationData":[TD([[subQ2,1.0]])],"derivedFrom":subQ1}),-1.0]])]});}
            var Q28;
            {var subQ0=sQuery(id+"F6.wireOp",EDGE,"E43.6.0.0");var subQ1=makeQuery(id+"F1.opExtrude","CAP_EDGE",EDGE,{"disambiguationData":[OSD([sQuery(id+"F0.wireOp",EDGE,"E33.20")])],"isStart":false});var subQ2=makeQuery(id+"F6.imprint","INTERSECT",VERTEX,{"derivedFrom":[subQ1,subQ0]});Q28=makeQuery(id+"F6.imprint","IMPRINT",FACE,{"disambiguationData":[TD([[makeQuery(id+"F6.imprint","IMPRINT",EDGE,{"disambiguationData":[TD([[subQ2,1.0]])],"derivedFrom":subQ1}),-1.0]])]});}
            var Q29;
            {var subQ0=sQuery(id+"F6.wireOp",EDGE,"E43.5.0.0");var subQ1=makeQuery(id+"F1.opExtrude","CAP_EDGE",EDGE,{"disambiguationData":[OSD([sQuery(id+"F0.wireOp",EDGE,"E33.20")])],"isStart":false});var subQ2=makeQuery(id+"F6.imprint","INTERSECT",VERTEX,{"derivedFrom":[subQ1,subQ0]});Q29=makeQuery(id+"F6.imprint","IMPRINT",FACE,{"disambiguationData":[TD([[makeQuery(id+"F6.imprint","IMPRINT",EDGE,{"disambiguationData":[TD([[subQ2,1.0]])],"derivedFrom":subQ1}),-1.0]])]});}
            var Q30;
            {var subQ0=sQuery(id+"F6.wireOp",EDGE,"E43.6.0.0");var subQ1=makeQuery(id+"F1.opExtrude","CAP_EDGE",EDGE,{"disambiguationData":[OSD([sQuery(id+"F0.wireOp",EDGE,"E33.12")])],"isStart":false});var subQ2=makeQuery(id+"F6.imprint","INTERSECT",VERTEX,{"derivedFrom":[subQ1,subQ0]});Q30=makeQuery(id+"F6.imprint","IMPRINT",FACE,{"disambiguationData":[TD([[makeQuery(id+"F6.imprint","IMPRINT",EDGE,{"disambiguationData":[TD([[subQ2,-1.0]])],"derivedFrom":subQ0}),-1.0]])]});}
            var Q31;
            {var subQ0=sQuery(id+"F6.wireOp",EDGE,"E43.5.0.0");var subQ1=makeQuery(id+"F1.opExtrude","CAP_EDGE",EDGE,{"disambiguationData":[OSD([sQuery(id+"F0.wireOp",EDGE,"E33.12")])],"isStart":false});var subQ2=makeQuery(id+"F6.imprint","INTERSECT",VERTEX,{"derivedFrom":[subQ1,subQ0]});Q31=makeQuery(id+"F6.imprint","IMPRINT",FACE,{"disambiguationData":[TD([[makeQuery(id+"F6.imprint","IMPRINT",EDGE,{"disambiguationData":[TD([[subQ2,-1.0]])],"derivedFrom":subQ0}),-1.0]])]});}
            var Q32;
            {var subQ0=sQuery(id+"F6.wireOp",EDGE,"E43.4.0.0");var subQ1=makeQuery(id+"F1.opExtrude","CAP_EDGE",EDGE,{"disambiguationData":[OSD([sQuery(id+"F0.wireOp",EDGE,"E33.12")])],"isStart":false});var subQ2=makeQuery(id+"F6.imprint","INTERSECT",VERTEX,{"derivedFrom":[subQ1,subQ0]});Q32=makeQuery(id+"F6.imprint","IMPRINT",FACE,{"disambiguationData":[TD([[makeQuery(id+"F6.imprint","IMPRINT",EDGE,{"disambiguationData":[TD([[subQ2,-1.0]])],"derivedFrom":subQ0}),-1.0]])]});}
            var Q33;
            {var subQ0=sQuery(id+"F6.wireOp",EDGE,"E43.7.0.0");var subQ1=makeQuery(id+"F1.opExtrude","CAP_EDGE",EDGE,{"disambiguationData":[OSD([sQuery(id+"F0.wireOp",EDGE,"E33.12")])],"isStart":false});var subQ2=makeQuery(id+"F6.imprint","INTERSECT",VERTEX,{"derivedFrom":[subQ1,subQ0]});Q33=makeQuery(id+"F6.imprint","IMPRINT",FACE,{"disambiguationData":[TD([[makeQuery(id+"F6.imprint","IMPRINT",EDGE,{"disambiguationData":[TD([[subQ2,-1.0]])],"derivedFrom":subQ0}),-1.0]])]});}
            var Q34;
            {var subQ0=sQuery(id+"F6.wireOp",EDGE,"E43.3.0.0");var subQ1=makeQuery(id+"F1.opExtrude","CAP_EDGE",EDGE,{"disambiguationData":[OSD([sQuery(id+"F0.wireOp",EDGE,"E33.12")])],"isStart":false});var subQ2=makeQuery(id+"F6.imprint","INTERSECT",VERTEX,{"derivedFrom":[subQ1,subQ0]});Q34=makeQuery(id+"F6.imprint","IMPRINT",FACE,{"disambiguationData":[TD([[makeQuery(id+"F6.imprint","IMPRINT",EDGE,{"disambiguationData":[TD([[subQ2,-1.0]])],"derivedFrom":subQ0}),-1.0]])]});}
            var Q35;
            {var subQ0=sQuery(id+"F6.wireOp",EDGE,"E43.2.0.0");var subQ1=makeQuery(id+"F1.opExtrude","CAP_EDGE",EDGE,{"disambiguationData":[OSD([sQuery(id+"F0.wireOp",EDGE,"E33.16")])],"isStart":false});var subQ2=makeQuery(id+"F6.imprint","INTERSECT",VERTEX,{"derivedFrom":[subQ1,subQ0]});Q35=makeQuery(id+"F6.imprint","IMPRINT",FACE,{"disambiguationData":[TD([[makeQuery(id+"F6.imprint","IMPRINT",EDGE,{"disambiguationData":[TD([[subQ2,-1.0]])],"derivedFrom":subQ0}),-1.0]])]});}
            var Q36;
            {var subQ0=sQuery(id+"F6.wireOp",EDGE,"E43.4.0.0");var subQ1=makeQuery(id+"F1.opExtrude","CAP_EDGE",EDGE,{"disambiguationData":[OSD([sQuery(id+"F0.wireOp",EDGE,"E33.20")])],"isStart":false});var subQ2=makeQuery(id+"F6.imprint","INTERSECT",VERTEX,{"derivedFrom":[subQ1,subQ0]});Q36=makeQuery(id+"F6.imprint","IMPRINT",FACE,{"disambiguationData":[TD([[makeQuery(id+"F6.imprint","IMPRINT",EDGE,{"disambiguationData":[TD([[subQ2,-1.0]])],"derivedFrom":subQ0}),-1.0]])]});}
            var Q37;
            {var subQ0=sQuery(id+"F6.wireOp",EDGE,"E43.13.0.0");var subQ1=makeQuery(id+"F1.opExtrude","CAP_EDGE",EDGE,{"disambiguationData":[OSD([sQuery(id+"F0.wireOp",EDGE,"E33.6")])],"isStart":false});var subQ2=makeQuery(id+"F6.imprint","INTERSECT",VERTEX,{"derivedFrom":[subQ1,subQ0]});Q37=makeQuery(id+"F6.imprint","IMPRINT",FACE,{"disambiguationData":[TD([[makeQuery(id+"F6.imprint","IMPRINT",EDGE,{"disambiguationData":[TD([[subQ2,-1.0]])],"derivedFrom":subQ0}),-1.0]])]});}
            var Q38;
            {var subQ0=sQuery(id+"F6.wireOp",EDGE,"E43.11.0.0");var subQ1=makeQuery(id+"F1.opExtrude","CAP_EDGE",EDGE,{"disambiguationData":[OSD([sQuery(id+"F0.wireOp",EDGE,"E33.15")])],"isStart":false});var subQ2=makeQuery(id+"F6.imprint","INTERSECT",VERTEX,{"derivedFrom":[subQ1,subQ0]});Q38=makeQuery(id+"F6.imprint","IMPRINT",FACE,{"disambiguationData":[TD([[makeQuery(id+"F6.imprint","IMPRINT",EDGE,{"disambiguationData":[TD([[subQ2,-1.0]])],"derivedFrom":subQ0}),-1.0]])]});}
            var Q39;
            {var subQ0=sQuery(id+"F6.wireOp",EDGE,"E43.11.0.0");var subQ1=makeQuery(id+"F1.opExtrude","CAP_EDGE",EDGE,{"disambiguationData":[OSD([sQuery(id+"F0.wireOp",EDGE,"E33.20")])],"isStart":false});var subQ2=makeQuery(id+"F6.imprint","INTERSECT",VERTEX,{"derivedFrom":[subQ1,subQ0]});Q39=makeQuery(id+"F6.imprint","IMPRINT",FACE,{"disambiguationData":[TD([[makeQuery(id+"F6.imprint","IMPRINT",EDGE,{"disambiguationData":[TD([[subQ2,1.0]])],"derivedFrom":subQ1}),-1.0]])]});}
            extrude(context, id + "F8", {"entities" : qUnion([Q0, Q1, Q2, Q3, Q4, Q5, Q6, Q7, Q8, Q9, Q10, Q11, Q12, Q13, Q14, Q15, Q16, Q17, Q18, Q19, Q20, Q21, Q22, Q23, Q24, Q25, Q26, Q27, Q28, Q29, Q30, Q31, Q32, Q33, Q34, Q35, Q36, Q37, Q38, Q39]), "operationType" : NewBodyOperationType.ADD, "oppositeDirection" : true, "depth" : 2 * mm, "offsetDistance" : 25 * mm});
        }
        {
            var Q0;
            {var subQ1=sQuery(id+"F0.wireOp",EDGE,"E33.1");Q0=makeQuery(id+"F2.imprint","IMPRINT",FACE,{"disambiguationData":[TD([[makeQuery(id+"F2.imprint","IMPRINT",EDGE,{"derivedFrom":makeQuery(id+"F1.opExtrude","CAP_EDGE",EDGE,{"disambiguationData":[OSD([subQ1])],"isStart":false})}),1.0]])]});}
            extrude(context, id + "F9", {"entities" : qUnion([Q0]), "operationType" : NewBodyOperationType.REMOVE, "oppositeDirection" : true, "depth" : 0.5 * mm, "offsetDistance" : 25 * mm});
        }
        {
            var Q0;
            {var subQ1=sQuery(id+"F0.wireOp",EDGE,"E33.1");Q0=makeQuery(id+"F0.imprint","IMPRINT",FACE,{"disambiguationData":[TD([[makeQuery(id+"F0.imprint","IMPRINT",EDGE,{"derivedFrom":subQ1}),1.0]])]});}
            extrude(context, id + "F10", {"entities" : qUnion([Q0]), "operationType" : NewBodyOperationType.REMOVE, "depth" : 0.5 * mm, "offsetDistance" : 25 * mm});
        }
        {
            var Q0;
            Q0=makeQuery(id+"F1.opExtrude","SWEPT_EDGE",EDGE,{"disambiguationData":[OSD([sQuery(id+"F0.wireOp",EDGE,"E30"),sQuery(id+"F0.wireOp",EDGE,"E33.1")])]});
            var Q1;
            Q1=makeQuery(id+"F10.boolean.opBoolean","COPY",EDGE,{"derivedFrom":makeQuery(id+"F10.opExtrude","SWEPT_EDGE",EDGE,{"disambiguationData":[OSD([sQuery(id+"F0.wireOp",EDGE,"E30"),sQuery(id+"F0.wireOp",EDGE,"E33.5")])]})});
            fillet(context, id + "F11", {"entities" : qUnion([Q0, Q1]), "tangentPropagation" : true, "radius" : 0.5 * mm, "defaultsChanged" : true, "vertexSettings" : [], "allowEdgeOverflow" : false});
        }
        {
            var Q0;
            {var subQ0=sQuery(id+"F0.wireOp",EDGE,"E33.5");var subQ1=sQuery(id+"F0.wireOp",EDGE,"E33.1");var subQ2=sQuery(id+"F0.wireOp",EDGE,"E30");var subQ3=sQuery(id+"F0.wireOp",EDGE,"E33.14");var subQ4=sQuery(id+"F0.wireOp",EDGE,"E33.13");var subQ5=sQuery(id+"F6.wireOp",EDGE,"E43.17.0.1");var subQ6=sQuery(id+"F0.wireOp",EDGE,"E33.3");var subQ7=sQuery(id+"F0.wireOp",EDGE,"E33.2");var subQ8=sQuery(id+"F6.wireOp",EDGE,"E43.17.0.0");var subQ9=sQuery(id+"F6.wireOp",EDGE,"E43.16.0.1");var subQ10=sQuery(id+"F6.wireOp",EDGE,"E43.16.0.0");var subQ11=sQuery(id+"F0.wireOp",EDGE,"E33.4");var subQ12=sQuery(id+"F6.wireOp",EDGE,"E43.15.0.1");var subQ13=sQuery(id+"F6.wireOp",EDGE,"E43.15.0.0");var subQ14=sQuery(id+"F6.wireOp",EDGE,"E43.14.0.1");var subQ15=sQuery(id+"F6.wireOp",EDGE,"E43.14.0.0");var subQ16=sQuery(id+"F6.wireOp",EDGE,"E43.13.0.1");var subQ17=sQuery(id+"F6.wireOp",EDGE,"E43.13.0.0");var subQ18=sQuery(id+"F0.wireOp",EDGE,"E33.7");var subQ19=sQuery(id+"F0.wireOp",EDGE,"E33.6");var subQ20=sQuery(id+"F0.wireOp",EDGE,"E33.15");var subQ21=sQuery(id+"F6.wireOp",EDGE,"E43.12.0.1");var subQ22=sQuery(id+"F6.wireOp",EDGE,"E43.12.0.0");var subQ23=sQuery(id+"F0.wireOp",EDGE,"E33.11");var subQ24=sQuery(id+"F0.wireOp",EDGE,"E33.10");var subQ25=sQuery(id+"F0.wireOp",EDGE,"E33.9");var subQ26=sQuery(id+"F0.wireOp",EDGE,"E33.8");var subQ27=sQuery(id+"F6.wireOp",EDGE,"E43.11.0.1");var subQ28=sQuery(id+"F6.wireOp",EDGE,"E43.11.0.0");var subQ29=sQuery(id+"F0.wireOp",EDGE,"E33.20");var subQ30=sQuery(id+"F0.wireOp",EDGE,"E33.19");var subQ31=sQuery(id+"F6.wireOp",EDGE,"E43.10.0.1");var subQ32=sQuery(id+"F6.wireOp",EDGE,"E43.10.0.0");var subQ33=sQuery(id+"F0.wireOp",EDGE,"E33.12");var subQ34=sQuery(id+"F6.wireOp",EDGE,"E43.9.0.1");var subQ35=sQuery(id+"F6.wireOp",EDGE,"E43.9.0.0");var subQ36=sQuery(id+"F0.wireOp",EDGE,"E33.18");var subQ37=sQuery(id+"F6.wireOp",EDGE,"E43.8.0.1");var subQ38=sQuery(id+"F6.wireOp",EDGE,"E43.8.0.0");var subQ39=sQuery(id+"F6.wireOp",EDGE,"E43.7.0.1");var subQ40=sQuery(id+"F6.wireOp",EDGE,"E43.7.0.0");var subQ41=sQuery(id+"F6.wireOp",EDGE,"E43.6.0.1");var subQ42=sQuery(id+"F6.wireOp",EDGE,"E43.6.0.0");var subQ43=sQuery(id+"F6.wireOp",EDGE,"E43.5.0.1");var subQ44=sQuery(id+"F6.wireOp",EDGE,"E43.5.0.0");var subQ45=sQuery(id+"F6.wireOp",EDGE,"E43.4.0.1");var subQ46=sQuery(id+"F6.wireOp",EDGE,"E43.4.0.0");var subQ47=sQuery(id+"F0.wireOp",EDGE,"E33.21");var subQ48=sQuery(id+"F0.wireOp",EDGE,"E33.16");var subQ49=sQuery(id+"F5.wireOp",EDGE,"E38.17.0.1");var subQ50=sQuery(id+"F5.wireOp",EDGE,"E38.17.0.0");var subQ51=sQuery(id+"F5.wireOp",EDGE,"E38.16.0.1");var subQ52=sQuery(id+"F5.wireOp",EDGE,"E38.16.0.0");var subQ53=sQuery(id+"F5.wireOp",EDGE,"E38.15.0.1");var subQ54=sQuery(id+"F5.wireOp",EDGE,"E38.15.0.0");var subQ55=sQuery(id+"F5.wireOp",EDGE,"E38.14.0.1");var subQ56=sQuery(id+"F5.wireOp",EDGE,"E38.14.0.0");var subQ57=sQuery(id+"F5.wireOp",EDGE,"E38.13.0.1");var subQ58=sQuery(id+"F5.wireOp",EDGE,"E38.13.0.0");var subQ59=sQuery(id+"F5.wireOp",EDGE,"E38.12.0.1");var subQ60=sQuery(id+"F5.wireOp",EDGE,"E38.12.0.0");var subQ61=sQuery(id+"F5.wireOp",EDGE,"E38.11.0.1");var subQ62=sQuery(id+"F5.wireOp",EDGE,"E38.11.0.0");var subQ63=sQuery(id+"F5.wireOp",EDGE,"E38.10.0.1");var subQ64=sQuery(id+"F5.wireOp",EDGE,"E38.10.0.0");var subQ65=sQuery(id+"F5.wireOp",EDGE,"E38.9.0.1");var subQ66=sQuery(id+"F5.wireOp",EDGE,"E38.9.0.0");var subQ67=sQuery(id+"F5.wireOp",EDGE,"E38.8.0.1");var subQ68=sQuery(id+"F5.wireOp",EDGE,"E38.8.0.0");var subQ69=sQuery(id+"F5.wireOp",EDGE,"E38.7.0.1");var subQ70=sQuery(id+"F5.wireOp",EDGE,"E38.7.0.0");var subQ71=sQuery(id+"F5.wireOp",EDGE,"E38.6.0.1");var subQ72=sQuery(id+"F5.wireOp",EDGE,"E38.6.0.0");var subQ73=sQuery(id+"F5.wireOp",EDGE,"E38.5.0.1");var subQ74=sQuery(id+"F5.wireOp",EDGE,"E38.5.0.0");var subQ75=sQuery(id+"F5.wireOp",EDGE,"E38.4.0.1");var subQ76=sQuery(id+"F5.wireOp",EDGE,"E38.4.0.0");var subQ77=sQuery(id+"F0.wireOp",EDGE,"E33.17");Q0=makeQuery(id+"F8.boolean.opBoolean","MERGE",FACE,{"derivedFrom":[makeQuery(id+"F7.boolean.opBoolean","MERGE",FACE,{"derivedFrom":[makeQuery(id+"F1.opExtrude","CAP_FACE",FACE,{"disambiguationData":[OSD([sQuery(id+"F0.wireOp",EDGE,"E0"),sQuery(id+"F0.wireOp",EDGE,"E1"),sQuery(id+"F0.wireOp",EDGE,"E2"),sQuery(id+"F0.wireOp",EDGE,"E3"),sQuery(id+"F0.wireOp",EDGE,"E4"),sQuery(id+"F0.wireOp",EDGE,"E5"),sQuery(id+"F0.wireOp",EDGE,"E6"),sQuery(id+"F0.wireOp",EDGE,"E10"),sQuery(id+"F0.wireOp",EDGE,"E11"),sQuery(id+"F0.wireOp",EDGE,"E12"),sQuery(id+"F0.wireOp",EDGE,"E13"),sQuery(id+"F0.wireOp",EDGE,"E15"),sQuery(id+"F0.wireOp",EDGE,"E16"),sQuery(id+"F0.wireOp",EDGE,"E17"),sQuery(id+"F0.wireOp",EDGE,"E18"),sQuery(id+"F0.wireOp",EDGE,"E19"),sQuery(id+"F0.wireOp",EDGE,"E20"),sQuery(id+"F0.wireOp",EDGE,"E21"),sQuery(id+"F0.wireOp",EDGE,"E22"),sQuery(id+"F0.wireOp",EDGE,"E29"),subQ2,subQ1,subQ7,subQ6,subQ11,subQ0,subQ19,subQ18,subQ26,subQ25,subQ24,subQ23,subQ33,subQ4,subQ3,subQ20,subQ48,subQ77,subQ36,subQ30,subQ29,subQ47])],"isStart":true}),makeQuery(id+"F7.opExtrude","CAP_FACE",FACE,{"disambiguationData":[OSD([subQ48,subQ77,sQuery(id+"F5.wireOp",EDGE,"E38.1.0.0"),sQuery(id+"F5.wireOp",EDGE,"E38.1.0.1")])],"isStart":false}),makeQuery(id+"F7.opExtrude","CAP_FACE",FACE,{"disambiguationData":[OSD([subQ33,subQ77,sQuery(id+"F5.wireOp",EDGE,"E38.2.0.0"),sQuery(id+"F5.wireOp",EDGE,"E38.2.0.1")])],"isStart":false}),makeQuery(id+"F7.opExtrude","CAP_FACE",FACE,{"disambiguationData":[OSD([subQ33,subQ36,sQuery(id+"F5.wireOp",EDGE,"E38.3.0.0"),sQuery(id+"F5.wireOp",EDGE,"E38.3.0.1")])],"isStart":false}),makeQuery(id+"F7.opExtrude","CAP_FACE",FACE,{"disambiguationData":[OSD([subQ0,subQ3,subQ20,subQ76,subQ75])],"isStart":false}),makeQuery(id+"F7.opExtrude","CAP_FACE",FACE,{"disambiguationData":[OSD([subQ33,subQ36,subQ76,subQ75])],"isStart":false}),makeQuery(id+"F7.opExtrude","CAP_FACE",FACE,{"disambiguationData":[OSD([subQ0,subQ3,subQ74,subQ73])],"isStart":false}),makeQuery(id+"F7.opExtrude","CAP_FACE",FACE,{"disambiguationData":[OSD([subQ33,subQ36,subQ74,subQ73])],"isStart":false}),makeQuery(id+"F7.opExtrude","CAP_FACE",FACE,{"disambiguationData":[OSD([subQ0,subQ3,subQ72,subQ71])],"isStart":false}),makeQuery(id+"F7.opExtrude","CAP_FACE",FACE,{"disambiguationData":[OSD([subQ33,subQ36,subQ72,subQ71])],"isStart":false}),makeQuery(id+"F7.opExtrude","CAP_FACE",FACE,{"disambiguationData":[OSD([subQ0,subQ3,subQ70,subQ69])],"isStart":false}),makeQuery(id+"F7.opExtrude","CAP_FACE",FACE,{"disambiguationData":[OSD([subQ33,subQ36,subQ70,subQ69])],"isStart":false}),makeQuery(id+"F7.opExtrude","CAP_FACE",FACE,{"disambiguationData":[OSD([subQ0,subQ3,subQ68,subQ67])],"isStart":false}),makeQuery(id+"F7.opExtrude","CAP_FACE",FACE,{"disambiguationData":[OSD([subQ33,subQ36,subQ68,subQ67])],"isStart":false}),makeQuery(id+"F7.opExtrude","CAP_FACE",FACE,{"disambiguationData":[OSD([subQ0,subQ3,subQ66,subQ65])],"isStart":false}),makeQuery(id+"F7.opExtrude","CAP_FACE",FACE,{"disambiguationData":[OSD([subQ4,subQ36,subQ66,subQ65])],"isStart":false}),makeQuery(id+"F7.opExtrude","CAP_FACE",FACE,{"disambiguationData":[OSD([subQ2,subQ0,subQ3,subQ64,subQ63])],"isStart":false}),makeQuery(id+"F7.opExtrude","CAP_FACE",FACE,{"disambiguationData":[OSD([subQ4,subQ30,subQ64,subQ63])],"isStart":false}),makeQuery(id+"F7.opExtrude","CAP_FACE",FACE,{"disambiguationData":[OSD([subQ29,subQ47,subQ63])],"isStart":false}),makeQuery(id+"F7.opExtrude","CAP_FACE",FACE,{"disambiguationData":[OSD([subQ2,subQ1,subQ62,subQ61])],"isStart":false}),makeQuery(id+"F7.opExtrude","CAP_FACE",FACE,{"disambiguationData":[OSD([subQ7,subQ30,subQ62,subQ61])],"isStart":false}),makeQuery(id+"F7.opExtrude","CAP_FACE",FACE,{"disambiguationData":[OSD([subQ29,subQ47,subQ62,subQ61])],"isStart":false}),makeQuery(id+"F7.opExtrude","CAP_FACE",FACE,{"disambiguationData":[OSD([subQ2,subQ1,subQ60,subQ59])],"isStart":false}),makeQuery(id+"F7.opExtrude","CAP_FACE",FACE,{"disambiguationData":[OSD([subQ7,subQ11,subQ19,subQ30,subQ60,subQ59])],"isStart":false}),makeQuery(id+"F7.opExtrude","CAP_FACE",FACE,{"disambiguationData":[OSD([subQ29,subQ47,subQ60,subQ59])],"isStart":false}),makeQuery(id+"F7.opExtrude","CAP_FACE",FACE,{"disambiguationData":[OSD([subQ7,subQ11,subQ58,subQ57])],"isStart":false}),makeQuery(id+"F7.opExtrude","CAP_FACE",FACE,{"disambiguationData":[OSD([subQ19,subQ30,subQ58,subQ57])],"isStart":false}),makeQuery(id+"F7.opExtrude","CAP_FACE",FACE,{"disambiguationData":[OSD([subQ26,subQ25,subQ24,subQ23,subQ29,subQ47,subQ58,subQ57])],"isStart":false}),makeQuery(id+"F7.opExtrude","CAP_FACE",FACE,{"disambiguationData":[OSD([subQ7,subQ11,subQ56,subQ55])],"isStart":false}),makeQuery(id+"F7.opExtrude","CAP_FACE",FACE,{"disambiguationData":[OSD([subQ19,subQ30,subQ56,subQ55])],"isStart":false}),makeQuery(id+"F7.opExtrude","CAP_FACE",FACE,{"disambiguationData":[OSD([subQ26,subQ25,subQ24,subQ23,subQ29,subQ56,subQ55])],"isStart":false}),makeQuery(id+"F7.opExtrude","CAP_FACE",FACE,{"disambiguationData":[OSD([subQ7,subQ11,subQ54,subQ53])],"isStart":false}),makeQuery(id+"F7.opExtrude","CAP_FACE",FACE,{"disambiguationData":[OSD([subQ19,subQ30,subQ54,subQ53])],"isStart":false}),makeQuery(id+"F7.opExtrude","CAP_FACE",FACE,{"disambiguationData":[OSD([subQ26,subQ25,subQ24,subQ23,subQ29,subQ54,subQ53])],"isStart":false}),makeQuery(id+"F7.opExtrude","CAP_FACE",FACE,{"disambiguationData":[OSD([subQ6,subQ11,subQ52,subQ51])],"isStart":false}),makeQuery(id+"F7.opExtrude","CAP_FACE",FACE,{"disambiguationData":[OSD([subQ19,subQ30,subQ52,subQ51])],"isStart":false}),makeQuery(id+"F7.opExtrude","CAP_FACE",FACE,{"disambiguationData":[OSD([subQ26,subQ25,subQ24,subQ23,subQ29,subQ52,subQ51])],"isStart":false}),makeQuery(id+"F7.opExtrude","CAP_FACE",FACE,{"disambiguationData":[OSD([subQ19,subQ30,subQ50,subQ49])],"isStart":false}),makeQuery(id+"F7.opExtrude","CAP_FACE",FACE,{"disambiguationData":[OSD([subQ26,subQ25,subQ24,subQ23,subQ29,subQ50,subQ49])],"isStart":false}),makeQuery(id+"F7.opExtrude","CAP_FACE",FACE,{"disambiguationData":[OSD([subQ19,subQ26,subQ25,subQ24,subQ23,sQuery(id+"F5.wireOp",EDGE,"E38.18.0.0"),sQuery(id+"F5.wireOp",EDGE,"E38.18.0.1")])],"isStart":false}),makeQuery(id+"F7.opExtrude","CAP_FACE",FACE,{"disambiguationData":[OSD([subQ19,subQ26,subQ25,subQ24,subQ23,sQuery(id+"F5.wireOp",EDGE,"E38.19.0.0"),sQuery(id+"F5.wireOp",EDGE,"E38.19.0.1")])],"isStart":false}),makeQuery(id+"F7.opExtrude","CAP_FACE",FACE,{"disambiguationData":[OSD([subQ18,subQ26,subQ25,subQ24,subQ23,sQuery(id+"F5.wireOp",EDGE,"E39.0.20.0"),sQuery(id+"F5.wireOp",EDGE,"E39.3.20.0")])],"isStart":false})]}),makeQuery(id+"F8.opExtrude","CAP_FACE",FACE,{"disambiguationData":[OSD([subQ48,subQ36,sQuery(id+"F6.wireOp",EDGE,"E43.2.0.0"),sQuery(id+"F6.wireOp",EDGE,"E43.2.0.1")])],"isStart":false}),makeQuery(id+"F8.opExtrude","CAP_FACE",FACE,{"disambiguationData":[OSD([subQ33,subQ36,sQuery(id+"F6.wireOp",EDGE,"E43.3.0.0"),sQuery(id+"F6.wireOp",EDGE,"E43.3.0.1")])],"isStart":false}),makeQuery(id+"F8.opExtrude","CAP_FACE",FACE,{"disambiguationData":[OSD([subQ33,subQ36,subQ46,subQ45])],"isStart":false}),makeQuery(id+"F8.opExtrude","CAP_FACE",FACE,{"disambiguationData":[OSD([subQ29,subQ47,subQ46,subQ45])],"isStart":false}),makeQuery(id+"F8.opExtrude","CAP_FACE",FACE,{"disambiguationData":[OSD([subQ33,subQ36,subQ44,subQ43])],"isStart":false}),makeQuery(id+"F8.opExtrude","CAP_FACE",FACE,{"disambiguationData":[OSD([subQ26,subQ25,subQ24,subQ23,subQ29,subQ44,subQ43])],"isStart":false}),makeQuery(id+"F8.opExtrude","CAP_FACE",FACE,{"disambiguationData":[OSD([subQ33,subQ36,subQ42,subQ41])],"isStart":false}),makeQuery(id+"F8.opExtrude","CAP_FACE",FACE,{"disambiguationData":[OSD([subQ26,subQ25,subQ24,subQ23,subQ29,subQ42,subQ41])],"isStart":false}),makeQuery(id+"F8.opExtrude","CAP_FACE",FACE,{"disambiguationData":[OSD([subQ33,subQ36,subQ40,subQ39])],"isStart":false}),makeQuery(id+"F8.opExtrude","CAP_FACE",FACE,{"disambiguationData":[OSD([subQ26,subQ25,subQ24,subQ23,subQ29,subQ40,subQ39])],"isStart":false}),makeQuery(id+"F8.opExtrude","CAP_FACE",FACE,{"disambiguationData":[OSD([subQ33,subQ36,subQ38,subQ37])],"isStart":false}),makeQuery(id+"F8.opExtrude","CAP_FACE",FACE,{"disambiguationData":[OSD([subQ26,subQ25,subQ24,subQ23,subQ29,subQ38,subQ37])],"isStart":false}),makeQuery(id+"F8.opExtrude","CAP_FACE",FACE,{"disambiguationData":[OSD([subQ33,subQ36,subQ35,subQ34])],"isStart":false}),makeQuery(id+"F8.opExtrude","CAP_FACE",FACE,{"disambiguationData":[OSD([subQ26,subQ25,subQ24,subQ23,subQ29,subQ35,subQ34])],"isStart":false}),makeQuery(id+"F8.opExtrude","CAP_FACE",FACE,{"disambiguationData":[OSD([subQ33,subQ30,subQ32,subQ31])],"isStart":false}),makeQuery(id+"F8.opExtrude","CAP_FACE",FACE,{"disambiguationData":[OSD([subQ26,subQ25,subQ24,subQ23,subQ29,subQ32,subQ31])],"isStart":false}),makeQuery(id+"F8.opExtrude","CAP_FACE",FACE,{"disambiguationData":[OSD([subQ3,subQ20,subQ28,subQ27])],"isStart":false}),makeQuery(id+"F8.opExtrude","CAP_FACE",FACE,{"disambiguationData":[OSD([subQ4,subQ30,subQ28,subQ27])],"isStart":false}),makeQuery(id+"F8.opExtrude","CAP_FACE",FACE,{"disambiguationData":[OSD([subQ26,subQ25,subQ24,subQ23,subQ29,subQ28,subQ27])],"isStart":false}),makeQuery(id+"F8.opExtrude","CAP_FACE",FACE,{"disambiguationData":[OSD([subQ3,subQ20,subQ22,subQ21])],"isStart":false}),makeQuery(id+"F8.opExtrude","CAP_FACE",FACE,{"disambiguationData":[OSD([subQ11,subQ4,subQ22,subQ21])],"isStart":false}),makeQuery(id+"F8.opExtrude","CAP_FACE",FACE,{"disambiguationData":[OSD([subQ19,subQ18,subQ26,subQ25,subQ24,subQ23,subQ22,subQ21])],"isStart":false}),makeQuery(id+"F8.opExtrude","CAP_FACE",FACE,{"disambiguationData":[OSD([subQ3,subQ20,subQ17,subQ16])],"isStart":false}),makeQuery(id+"F8.opExtrude","CAP_FACE",FACE,{"disambiguationData":[OSD([subQ1,subQ4,subQ17,subQ16])],"isStart":false}),makeQuery(id+"F8.opExtrude","CAP_FACE",FACE,{"disambiguationData":[OSD([subQ7,subQ11,subQ17,subQ16])],"isStart":false}),makeQuery(id+"F8.opExtrude","CAP_FACE",FACE,{"disambiguationData":[OSD([subQ19,subQ18,subQ17,subQ16])],"isStart":false}),makeQuery(id+"F8.opExtrude","CAP_FACE",FACE,{"disambiguationData":[OSD([subQ0,subQ3,subQ15,subQ14])],"isStart":false}),makeQuery(id+"F8.opExtrude","CAP_FACE",FACE,{"disambiguationData":[OSD([subQ1,subQ4,subQ15,subQ14])],"isStart":false}),makeQuery(id+"F8.opExtrude","CAP_FACE",FACE,{"disambiguationData":[OSD([subQ7,subQ11,subQ15,subQ14])],"isStart":false}),makeQuery(id+"F8.opExtrude","CAP_FACE",FACE,{"disambiguationData":[OSD([subQ0,subQ3,subQ13,subQ12])],"isStart":false}),makeQuery(id+"F8.opExtrude","CAP_FACE",FACE,{"disambiguationData":[OSD([subQ1,subQ4,subQ13,subQ12])],"isStart":false}),makeQuery(id+"F8.opExtrude","CAP_FACE",FACE,{"disambiguationData":[OSD([subQ7,subQ11,subQ13,subQ12])],"isStart":false}),makeQuery(id+"F8.opExtrude","CAP_FACE",FACE,{"disambiguationData":[OSD([subQ0,subQ3,subQ10,subQ9])],"isStart":false}),makeQuery(id+"F8.opExtrude","CAP_FACE",FACE,{"disambiguationData":[OSD([subQ1,subQ4,subQ10,subQ9])],"isStart":false}),makeQuery(id+"F8.opExtrude","CAP_FACE",FACE,{"disambiguationData":[OSD([subQ7,subQ6,subQ11,subQ10,subQ9])],"isStart":false}),makeQuery(id+"F8.opExtrude","CAP_FACE",FACE,{"disambiguationData":[OSD([subQ0,subQ3,subQ8,subQ5])],"isStart":false}),makeQuery(id+"F8.opExtrude","CAP_FACE",FACE,{"disambiguationData":[OSD([subQ1,subQ4,subQ8,subQ5])],"isStart":false}),makeQuery(id+"F8.opExtrude","CAP_FACE",FACE,{"disambiguationData":[OSD([subQ7,subQ6,subQ5])],"isStart":false}),makeQuery(id+"F8.opExtrude","CAP_FACE",FACE,{"disambiguationData":[OSD([subQ1,subQ0,subQ4,subQ3,sQuery(id+"F6.wireOp",EDGE,"E43.18.0.0"),sQuery(id+"F6.wireOp",EDGE,"E43.18.0.1")])],"isStart":false}),makeQuery(id+"F8.opExtrude","CAP_FACE",FACE,{"disambiguationData":[OSD([subQ2,subQ1,subQ0,sQuery(id+"F6.wireOp",EDGE,"E43.19.0.0"),sQuery(id+"F6.wireOp",EDGE,"E43.19.0.1")])],"isStart":false})]});}
            var Q1;
            {var subQ0=sQuery(id+"F0.wireOp",EDGE,"E33.5");var subQ1=sQuery(id+"F0.wireOp",EDGE,"E33.1");var subQ2=sQuery(id+"F0.wireOp",EDGE,"E30");var subQ3=sQuery(id+"F0.wireOp",EDGE,"E33.14");var subQ4=sQuery(id+"F0.wireOp",EDGE,"E33.13");var subQ5=sQuery(id+"F6.wireOp",EDGE,"E43.17.0.1");var subQ6=sQuery(id+"F0.wireOp",EDGE,"E33.3");var subQ7=sQuery(id+"F0.wireOp",EDGE,"E33.2");var subQ8=sQuery(id+"F6.wireOp",EDGE,"E43.17.0.0");var subQ9=sQuery(id+"F6.wireOp",EDGE,"E43.16.0.1");var subQ10=sQuery(id+"F6.wireOp",EDGE,"E43.16.0.0");var subQ11=sQuery(id+"F0.wireOp",EDGE,"E33.4");var subQ12=sQuery(id+"F6.wireOp",EDGE,"E43.15.0.1");var subQ13=sQuery(id+"F6.wireOp",EDGE,"E43.15.0.0");var subQ14=sQuery(id+"F6.wireOp",EDGE,"E43.14.0.1");var subQ15=sQuery(id+"F6.wireOp",EDGE,"E43.14.0.0");var subQ16=sQuery(id+"F6.wireOp",EDGE,"E43.13.0.1");var subQ17=sQuery(id+"F6.wireOp",EDGE,"E43.13.0.0");var subQ18=sQuery(id+"F0.wireOp",EDGE,"E33.7");var subQ19=sQuery(id+"F0.wireOp",EDGE,"E33.6");var subQ20=sQuery(id+"F0.wireOp",EDGE,"E33.15");var subQ21=sQuery(id+"F6.wireOp",EDGE,"E43.12.0.1");var subQ22=sQuery(id+"F6.wireOp",EDGE,"E43.12.0.0");var subQ23=sQuery(id+"F0.wireOp",EDGE,"E33.11");var subQ24=sQuery(id+"F0.wireOp",EDGE,"E33.10");var subQ25=sQuery(id+"F0.wireOp",EDGE,"E33.9");var subQ26=sQuery(id+"F0.wireOp",EDGE,"E33.8");var subQ27=sQuery(id+"F6.wireOp",EDGE,"E43.11.0.1");var subQ28=sQuery(id+"F6.wireOp",EDGE,"E43.11.0.0");var subQ29=sQuery(id+"F0.wireOp",EDGE,"E33.20");var subQ30=sQuery(id+"F0.wireOp",EDGE,"E33.19");var subQ31=sQuery(id+"F6.wireOp",EDGE,"E43.10.0.1");var subQ32=sQuery(id+"F6.wireOp",EDGE,"E43.10.0.0");var subQ33=sQuery(id+"F0.wireOp",EDGE,"E33.12");var subQ34=sQuery(id+"F6.wireOp",EDGE,"E43.9.0.1");var subQ35=sQuery(id+"F6.wireOp",EDGE,"E43.9.0.0");var subQ36=sQuery(id+"F0.wireOp",EDGE,"E33.18");var subQ37=sQuery(id+"F6.wireOp",EDGE,"E43.8.0.1");var subQ38=sQuery(id+"F6.wireOp",EDGE,"E43.8.0.0");var subQ39=sQuery(id+"F6.wireOp",EDGE,"E43.7.0.1");var subQ40=sQuery(id+"F6.wireOp",EDGE,"E43.7.0.0");var subQ41=sQuery(id+"F6.wireOp",EDGE,"E43.6.0.1");var subQ42=sQuery(id+"F6.wireOp",EDGE,"E43.6.0.0");var subQ43=sQuery(id+"F6.wireOp",EDGE,"E43.5.0.1");var subQ44=sQuery(id+"F6.wireOp",EDGE,"E43.5.0.0");var subQ45=sQuery(id+"F6.wireOp",EDGE,"E43.4.0.1");var subQ46=sQuery(id+"F6.wireOp",EDGE,"E43.4.0.0");var subQ47=sQuery(id+"F0.wireOp",EDGE,"E33.21");var subQ48=sQuery(id+"F0.wireOp",EDGE,"E33.16");var subQ49=sQuery(id+"F5.wireOp",EDGE,"E38.17.0.1");var subQ50=sQuery(id+"F5.wireOp",EDGE,"E38.17.0.0");var subQ51=sQuery(id+"F5.wireOp",EDGE,"E38.16.0.1");var subQ52=sQuery(id+"F5.wireOp",EDGE,"E38.16.0.0");var subQ53=sQuery(id+"F5.wireOp",EDGE,"E38.15.0.1");var subQ54=sQuery(id+"F5.wireOp",EDGE,"E38.15.0.0");var subQ55=sQuery(id+"F5.wireOp",EDGE,"E38.14.0.1");var subQ56=sQuery(id+"F5.wireOp",EDGE,"E38.14.0.0");var subQ57=sQuery(id+"F5.wireOp",EDGE,"E38.13.0.1");var subQ58=sQuery(id+"F5.wireOp",EDGE,"E38.13.0.0");var subQ59=sQuery(id+"F5.wireOp",EDGE,"E38.12.0.1");var subQ60=sQuery(id+"F5.wireOp",EDGE,"E38.12.0.0");var subQ61=sQuery(id+"F5.wireOp",EDGE,"E38.11.0.1");var subQ62=sQuery(id+"F5.wireOp",EDGE,"E38.11.0.0");var subQ63=sQuery(id+"F5.wireOp",EDGE,"E38.10.0.1");var subQ64=sQuery(id+"F5.wireOp",EDGE,"E38.10.0.0");var subQ65=sQuery(id+"F5.wireOp",EDGE,"E38.9.0.1");var subQ66=sQuery(id+"F5.wireOp",EDGE,"E38.9.0.0");var subQ67=sQuery(id+"F5.wireOp",EDGE,"E38.8.0.1");var subQ68=sQuery(id+"F5.wireOp",EDGE,"E38.8.0.0");var subQ69=sQuery(id+"F5.wireOp",EDGE,"E38.7.0.1");var subQ70=sQuery(id+"F5.wireOp",EDGE,"E38.7.0.0");var subQ71=sQuery(id+"F5.wireOp",EDGE,"E38.6.0.1");var subQ72=sQuery(id+"F5.wireOp",EDGE,"E38.6.0.0");var subQ73=sQuery(id+"F5.wireOp",EDGE,"E38.5.0.1");var subQ74=sQuery(id+"F5.wireOp",EDGE,"E38.5.0.0");var subQ75=sQuery(id+"F5.wireOp",EDGE,"E38.4.0.1");var subQ76=sQuery(id+"F5.wireOp",EDGE,"E38.4.0.0");var subQ77=sQuery(id+"F0.wireOp",EDGE,"E33.17");Q1=makeQuery(id+"F8.boolean.opBoolean","MERGE",FACE,{"derivedFrom":[makeQuery(id+"F7.boolean.opBoolean","MERGE",FACE,{"derivedFrom":[makeQuery(id+"F1.opExtrude","CAP_FACE",FACE,{"disambiguationData":[OSD([sQuery(id+"F0.wireOp",EDGE,"E0"),sQuery(id+"F0.wireOp",EDGE,"E1"),sQuery(id+"F0.wireOp",EDGE,"E2"),sQuery(id+"F0.wireOp",EDGE,"E3"),sQuery(id+"F0.wireOp",EDGE,"E4"),sQuery(id+"F0.wireOp",EDGE,"E5"),sQuery(id+"F0.wireOp",EDGE,"E6"),sQuery(id+"F0.wireOp",EDGE,"E10"),sQuery(id+"F0.wireOp",EDGE,"E11"),sQuery(id+"F0.wireOp",EDGE,"E12"),sQuery(id+"F0.wireOp",EDGE,"E13"),sQuery(id+"F0.wireOp",EDGE,"E15"),sQuery(id+"F0.wireOp",EDGE,"E16"),sQuery(id+"F0.wireOp",EDGE,"E17"),sQuery(id+"F0.wireOp",EDGE,"E18"),sQuery(id+"F0.wireOp",EDGE,"E19"),sQuery(id+"F0.wireOp",EDGE,"E20"),sQuery(id+"F0.wireOp",EDGE,"E21"),sQuery(id+"F0.wireOp",EDGE,"E22"),sQuery(id+"F0.wireOp",EDGE,"E29"),subQ2,subQ1,subQ7,subQ6,subQ11,subQ0,subQ19,subQ18,subQ26,subQ25,subQ24,subQ23,subQ33,subQ4,subQ3,subQ20,subQ48,subQ77,subQ36,subQ30,subQ29,subQ47])],"isStart":false}),makeQuery(id+"F7.opExtrude","CAP_FACE",FACE,{"disambiguationData":[OSD([subQ48,subQ77,sQuery(id+"F5.wireOp",EDGE,"E38.1.0.0"),sQuery(id+"F5.wireOp",EDGE,"E38.1.0.1")])],"isStart":true}),makeQuery(id+"F7.opExtrude","CAP_FACE",FACE,{"disambiguationData":[OSD([subQ33,subQ77,sQuery(id+"F5.wireOp",EDGE,"E38.2.0.0"),sQuery(id+"F5.wireOp",EDGE,"E38.2.0.1")])],"isStart":true}),makeQuery(id+"F7.opExtrude","CAP_FACE",FACE,{"disambiguationData":[OSD([subQ33,subQ36,sQuery(id+"F5.wireOp",EDGE,"E38.3.0.0"),sQuery(id+"F5.wireOp",EDGE,"E38.3.0.1")])],"isStart":true}),makeQuery(id+"F7.opExtrude","CAP_FACE",FACE,{"disambiguationData":[OSD([subQ0,subQ3,subQ20,subQ76,subQ75])],"isStart":true}),makeQuery(id+"F7.opExtrude","CAP_FACE",FACE,{"disambiguationData":[OSD([subQ33,subQ36,subQ76,subQ75])],"isStart":true}),makeQuery(id+"F7.opExtrude","CAP_FACE",FACE,{"disambiguationData":[OSD([subQ0,subQ3,subQ74,subQ73])],"isStart":true}),makeQuery(id+"F7.opExtrude","CAP_FACE",FACE,{"disambiguationData":[OSD([subQ33,subQ36,subQ74,subQ73])],"isStart":true}),makeQuery(id+"F7.opExtrude","CAP_FACE",FACE,{"disambiguationData":[OSD([subQ0,subQ3,subQ72,subQ71])],"isStart":true}),makeQuery(id+"F7.opExtrude","CAP_FACE",FACE,{"disambiguationData":[OSD([subQ33,subQ36,subQ72,subQ71])],"isStart":true}),makeQuery(id+"F7.opExtrude","CAP_FACE",FACE,{"disambiguationData":[OSD([subQ0,subQ3,subQ70,subQ69])],"isStart":true}),makeQuery(id+"F7.opExtrude","CAP_FACE",FACE,{"disambiguationData":[OSD([subQ33,subQ36,subQ70,subQ69])],"isStart":true}),makeQuery(id+"F7.opExtrude","CAP_FACE",FACE,{"disambiguationData":[OSD([subQ0,subQ3,subQ68,subQ67])],"isStart":true}),makeQuery(id+"F7.opExtrude","CAP_FACE",FACE,{"disambiguationData":[OSD([subQ33,subQ36,subQ68,subQ67])],"isStart":true}),makeQuery(id+"F7.opExtrude","CAP_FACE",FACE,{"disambiguationData":[OSD([subQ0,subQ3,subQ66,subQ65])],"isStart":true}),makeQuery(id+"F7.opExtrude","CAP_FACE",FACE,{"disambiguationData":[OSD([subQ4,subQ36,subQ66,subQ65])],"isStart":true}),makeQuery(id+"F7.opExtrude","CAP_FACE",FACE,{"disambiguationData":[OSD([subQ2,subQ0,subQ3,subQ64,subQ63])],"isStart":true}),makeQuery(id+"F7.opExtrude","CAP_FACE",FACE,{"disambiguationData":[OSD([subQ4,subQ30,subQ64,subQ63])],"isStart":true}),makeQuery(id+"F7.opExtrude","CAP_FACE",FACE,{"disambiguationData":[OSD([subQ29,subQ47,subQ63])],"isStart":true}),makeQuery(id+"F7.opExtrude","CAP_FACE",FACE,{"disambiguationData":[OSD([subQ2,subQ1,subQ62,subQ61])],"isStart":true}),makeQuery(id+"F7.opExtrude","CAP_FACE",FACE,{"disambiguationData":[OSD([subQ7,subQ30,subQ62,subQ61])],"isStart":true}),makeQuery(id+"F7.opExtrude","CAP_FACE",FACE,{"disambiguationData":[OSD([subQ29,subQ47,subQ62,subQ61])],"isStart":true}),makeQuery(id+"F7.opExtrude","CAP_FACE",FACE,{"disambiguationData":[OSD([subQ2,subQ1,subQ60,subQ59])],"isStart":true}),makeQuery(id+"F7.opExtrude","CAP_FACE",FACE,{"disambiguationData":[OSD([subQ7,subQ11,subQ19,subQ30,subQ60,subQ59])],"isStart":true}),makeQuery(id+"F7.opExtrude","CAP_FACE",FACE,{"disambiguationData":[OSD([subQ29,subQ47,subQ60,subQ59])],"isStart":true}),makeQuery(id+"F7.opExtrude","CAP_FACE",FACE,{"disambiguationData":[OSD([subQ7,subQ11,subQ58,subQ57])],"isStart":true}),makeQuery(id+"F7.opExtrude","CAP_FACE",FACE,{"disambiguationData":[OSD([subQ19,subQ30,subQ58,subQ57])],"isStart":true}),makeQuery(id+"F7.opExtrude","CAP_FACE",FACE,{"disambiguationData":[OSD([subQ26,subQ25,subQ24,subQ23,subQ29,subQ47,subQ58,subQ57])],"isStart":true}),makeQuery(id+"F7.opExtrude","CAP_FACE",FACE,{"disambiguationData":[OSD([subQ7,subQ11,subQ56,subQ55])],"isStart":true}),makeQuery(id+"F7.opExtrude","CAP_FACE",FACE,{"disambiguationData":[OSD([subQ19,subQ30,subQ56,subQ55])],"isStart":true}),makeQuery(id+"F7.opExtrude","CAP_FACE",FACE,{"disambiguationData":[OSD([subQ26,subQ25,subQ24,subQ23,subQ29,subQ56,subQ55])],"isStart":true}),makeQuery(id+"F7.opExtrude","CAP_FACE",FACE,{"disambiguationData":[OSD([subQ7,subQ11,subQ54,subQ53])],"isStart":true}),makeQuery(id+"F7.opExtrude","CAP_FACE",FACE,{"disambiguationData":[OSD([subQ19,subQ30,subQ54,subQ53])],"isStart":true}),makeQuery(id+"F7.opExtrude","CAP_FACE",FACE,{"disambiguationData":[OSD([subQ26,subQ25,subQ24,subQ23,subQ29,subQ54,subQ53])],"isStart":true}),makeQuery(id+"F7.opExtrude","CAP_FACE",FACE,{"disambiguationData":[OSD([subQ6,subQ11,subQ52,subQ51])],"isStart":true}),makeQuery(id+"F7.opExtrude","CAP_FACE",FACE,{"disambiguationData":[OSD([subQ19,subQ30,subQ52,subQ51])],"isStart":true}),makeQuery(id+"F7.opExtrude","CAP_FACE",FACE,{"disambiguationData":[OSD([subQ26,subQ25,subQ24,subQ23,subQ29,subQ52,subQ51])],"isStart":true}),makeQuery(id+"F7.opExtrude","CAP_FACE",FACE,{"disambiguationData":[OSD([subQ19,subQ30,subQ50,subQ49])],"isStart":true}),makeQuery(id+"F7.opExtrude","CAP_FACE",FACE,{"disambiguationData":[OSD([subQ26,subQ25,subQ24,subQ23,subQ29,subQ50,subQ49])],"isStart":true}),makeQuery(id+"F7.opExtrude","CAP_FACE",FACE,{"disambiguationData":[OSD([subQ19,subQ26,subQ25,subQ24,subQ23,sQuery(id+"F5.wireOp",EDGE,"E38.18.0.0"),sQuery(id+"F5.wireOp",EDGE,"E38.18.0.1")])],"isStart":true}),makeQuery(id+"F7.opExtrude","CAP_FACE",FACE,{"disambiguationData":[OSD([subQ19,subQ26,subQ25,subQ24,subQ23,sQuery(id+"F5.wireOp",EDGE,"E38.19.0.0"),sQuery(id+"F5.wireOp",EDGE,"E38.19.0.1")])],"isStart":true}),makeQuery(id+"F7.opExtrude","CAP_FACE",FACE,{"disambiguationData":[OSD([subQ18,subQ26,subQ25,subQ24,subQ23,sQuery(id+"F5.wireOp",EDGE,"E39.0.20.0"),sQuery(id+"F5.wireOp",EDGE,"E39.3.20.0")])],"isStart":true})]}),makeQuery(id+"F8.opExtrude","CAP_FACE",FACE,{"disambiguationData":[OSD([subQ48,subQ36,sQuery(id+"F6.wireOp",EDGE,"E43.2.0.0"),sQuery(id+"F6.wireOp",EDGE,"E43.2.0.1")])],"isStart":true}),makeQuery(id+"F8.opExtrude","CAP_FACE",FACE,{"disambiguationData":[OSD([subQ33,subQ36,sQuery(id+"F6.wireOp",EDGE,"E43.3.0.0"),sQuery(id+"F6.wireOp",EDGE,"E43.3.0.1")])],"isStart":true}),makeQuery(id+"F8.opExtrude","CAP_FACE",FACE,{"disambiguationData":[OSD([subQ33,subQ36,subQ46,subQ45])],"isStart":true}),makeQuery(id+"F8.opExtrude","CAP_FACE",FACE,{"disambiguationData":[OSD([subQ29,subQ47,subQ46,subQ45])],"isStart":true}),makeQuery(id+"F8.opExtrude","CAP_FACE",FACE,{"disambiguationData":[OSD([subQ33,subQ36,subQ44,subQ43])],"isStart":true}),makeQuery(id+"F8.opExtrude","CAP_FACE",FACE,{"disambiguationData":[OSD([subQ26,subQ25,subQ24,subQ23,subQ29,subQ44,subQ43])],"isStart":true}),makeQuery(id+"F8.opExtrude","CAP_FACE",FACE,{"disambiguationData":[OSD([subQ33,subQ36,subQ42,subQ41])],"isStart":true}),makeQuery(id+"F8.opExtrude","CAP_FACE",FACE,{"disambiguationData":[OSD([subQ26,subQ25,subQ24,subQ23,subQ29,subQ42,subQ41])],"isStart":true}),makeQuery(id+"F8.opExtrude","CAP_FACE",FACE,{"disambiguationData":[OSD([subQ33,subQ36,subQ40,subQ39])],"isStart":true}),makeQuery(id+"F8.opExtrude","CAP_FACE",FACE,{"disambiguationData":[OSD([subQ26,subQ25,subQ24,subQ23,subQ29,subQ40,subQ39])],"isStart":true}),makeQuery(id+"F8.opExtrude","CAP_FACE",FACE,{"disambiguationData":[OSD([subQ33,subQ36,subQ38,subQ37])],"isStart":true}),makeQuery(id+"F8.opExtrude","CAP_FACE",FACE,{"disambiguationData":[OSD([subQ26,subQ25,subQ24,subQ23,subQ29,subQ38,subQ37])],"isStart":true}),makeQuery(id+"F8.opExtrude","CAP_FACE",FACE,{"disambiguationData":[OSD([subQ33,subQ36,subQ35,subQ34])],"isStart":true}),makeQuery(id+"F8.opExtrude","CAP_FACE",FACE,{"disambiguationData":[OSD([subQ26,subQ25,subQ24,subQ23,subQ29,subQ35,subQ34])],"isStart":true}),makeQuery(id+"F8.opExtrude","CAP_FACE",FACE,{"disambiguationData":[OSD([subQ33,subQ30,subQ32,subQ31])],"isStart":true}),makeQuery(id+"F8.opExtrude","CAP_FACE",FACE,{"disambiguationData":[OSD([subQ26,subQ25,subQ24,subQ23,subQ29,subQ32,subQ31])],"isStart":true}),makeQuery(id+"F8.opExtrude","CAP_FACE",FACE,{"disambiguationData":[OSD([subQ3,subQ20,subQ28,subQ27])],"isStart":true}),makeQuery(id+"F8.opExtrude","CAP_FACE",FACE,{"disambiguationData":[OSD([subQ4,subQ30,subQ28,subQ27])],"isStart":true}),makeQuery(id+"F8.opExtrude","CAP_FACE",FACE,{"disambiguationData":[OSD([subQ26,subQ25,subQ24,subQ23,subQ29,subQ28,subQ27])],"isStart":true}),makeQuery(id+"F8.opExtrude","CAP_FACE",FACE,{"disambiguationData":[OSD([subQ3,subQ20,subQ22,subQ21])],"isStart":true}),makeQuery(id+"F8.opExtrude","CAP_FACE",FACE,{"disambiguationData":[OSD([subQ11,subQ4,subQ22,subQ21])],"isStart":true}),makeQuery(id+"F8.opExtrude","CAP_FACE",FACE,{"disambiguationData":[OSD([subQ19,subQ18,subQ26,subQ25,subQ24,subQ23,subQ22,subQ21])],"isStart":true}),makeQuery(id+"F8.opExtrude","CAP_FACE",FACE,{"disambiguationData":[OSD([subQ3,subQ20,subQ17,subQ16])],"isStart":true}),makeQuery(id+"F8.opExtrude","CAP_FACE",FACE,{"disambiguationData":[OSD([subQ1,subQ4,subQ17,subQ16])],"isStart":true}),makeQuery(id+"F8.opExtrude","CAP_FACE",FACE,{"disambiguationData":[OSD([subQ7,subQ11,subQ17,subQ16])],"isStart":true}),makeQuery(id+"F8.opExtrude","CAP_FACE",FACE,{"disambiguationData":[OSD([subQ19,subQ18,subQ17,subQ16])],"isStart":true}),makeQuery(id+"F8.opExtrude","CAP_FACE",FACE,{"disambiguationData":[OSD([subQ0,subQ3,subQ15,subQ14])],"isStart":true}),makeQuery(id+"F8.opExtrude","CAP_FACE",FACE,{"disambiguationData":[OSD([subQ1,subQ4,subQ15,subQ14])],"isStart":true}),makeQuery(id+"F8.opExtrude","CAP_FACE",FACE,{"disambiguationData":[OSD([subQ7,subQ11,subQ15,subQ14])],"isStart":true}),makeQuery(id+"F8.opExtrude","CAP_FACE",FACE,{"disambiguationData":[OSD([subQ0,subQ3,subQ13,subQ12])],"isStart":true}),makeQuery(id+"F8.opExtrude","CAP_FACE",FACE,{"disambiguationData":[OSD([subQ1,subQ4,subQ13,subQ12])],"isStart":true}),makeQuery(id+"F8.opExtrude","CAP_FACE",FACE,{"disambiguationData":[OSD([subQ7,subQ11,subQ13,subQ12])],"isStart":true}),makeQuery(id+"F8.opExtrude","CAP_FACE",FACE,{"disambiguationData":[OSD([subQ0,subQ3,subQ10,subQ9])],"isStart":true}),makeQuery(id+"F8.opExtrude","CAP_FACE",FACE,{"disambiguationData":[OSD([subQ1,subQ4,subQ10,subQ9])],"isStart":true}),makeQuery(id+"F8.opExtrude","CAP_FACE",FACE,{"disambiguationData":[OSD([subQ7,subQ6,subQ11,subQ10,subQ9])],"isStart":true}),makeQuery(id+"F8.opExtrude","CAP_FACE",FACE,{"disambiguationData":[OSD([subQ0,subQ3,subQ8,subQ5])],"isStart":true}),makeQuery(id+"F8.opExtrude","CAP_FACE",FACE,{"disambiguationData":[OSD([subQ1,subQ4,subQ8,subQ5])],"isStart":true}),makeQuery(id+"F8.opExtrude","CAP_FACE",FACE,{"disambiguationData":[OSD([subQ7,subQ6,subQ5])],"isStart":true}),makeQuery(id+"F8.opExtrude","CAP_FACE",FACE,{"disambiguationData":[OSD([subQ1,subQ0,subQ4,subQ3,sQuery(id+"F6.wireOp",EDGE,"E43.18.0.0"),sQuery(id+"F6.wireOp",EDGE,"E43.18.0.1")])],"isStart":true}),makeQuery(id+"F8.opExtrude","CAP_FACE",FACE,{"disambiguationData":[OSD([subQ2,subQ1,subQ0,sQuery(id+"F6.wireOp",EDGE,"E43.19.0.0"),sQuery(id+"F6.wireOp",EDGE,"E43.19.0.1")])],"isStart":true})]});}
            fillet(context, id + "F12", {"entities" : qUnion([Q0, Q1]), "tangentPropagation" : true, "radius" : 0.3 * mm, "defaultsChanged" : false, "vertexSettings" : [], "allowEdgeOverflow" : false});
        }
    });
